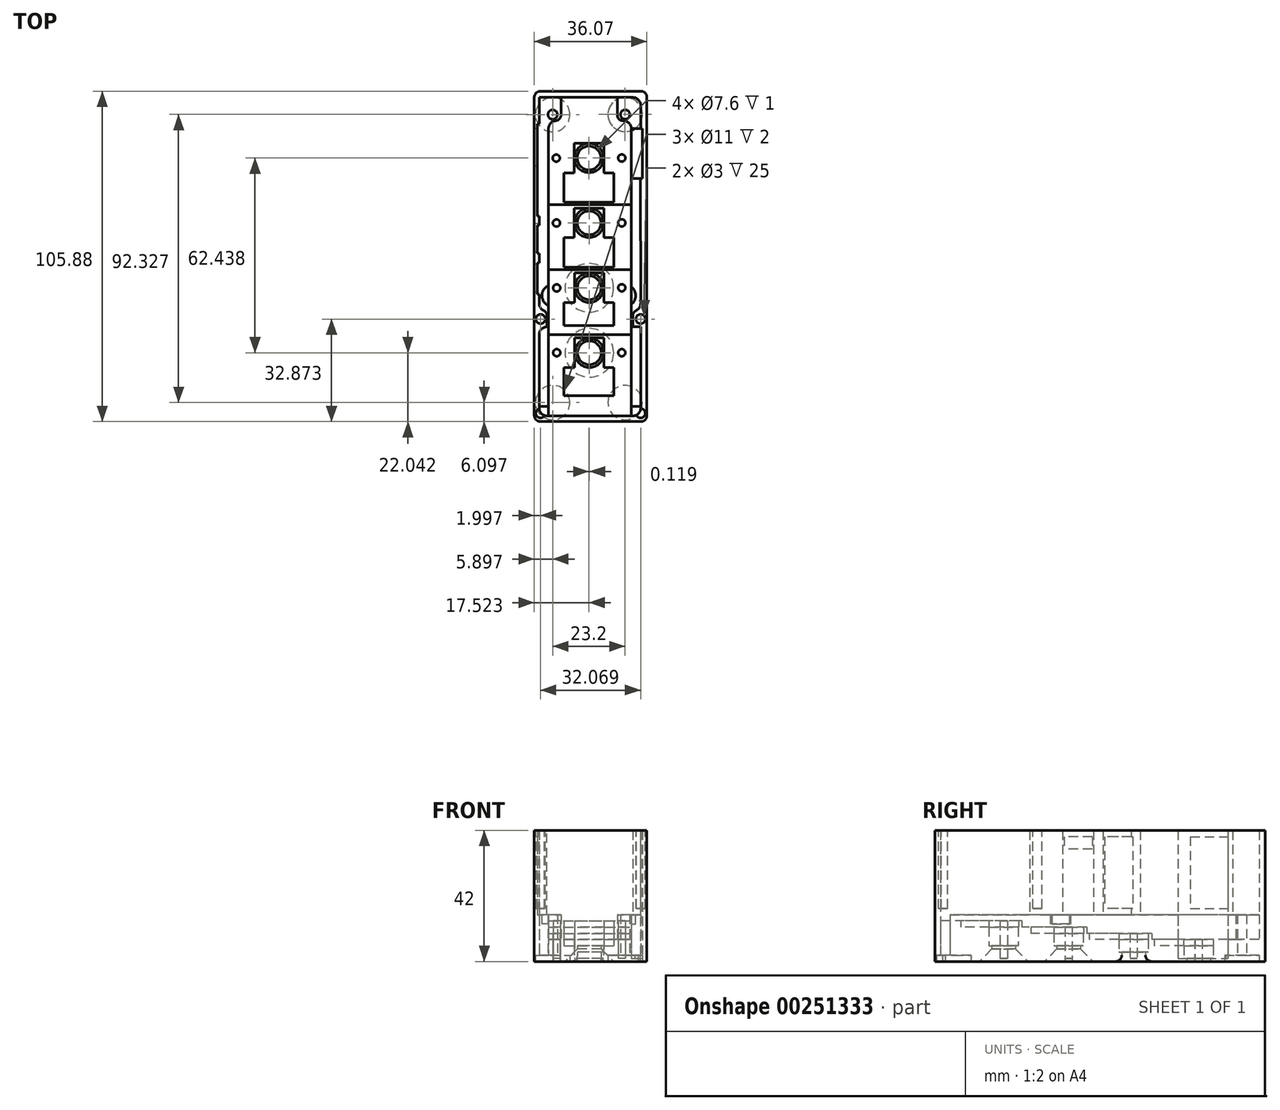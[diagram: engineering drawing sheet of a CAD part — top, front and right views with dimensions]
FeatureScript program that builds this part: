
annotation { "Feature Type Name" : "Feature", "Feature Type Description" : "" }
export const myFeature = defineFeature(function(context is Context, id is Id, definition is map)
    precondition{}
    {
        {
            var Q0;
            Q0=qCreatedBy(makeId("Top.planeOp"),FACE);
            var sketch = newSketch(context, id + "F0", { "sketchPlane" : qUnion([Q0])});
            skLineSegment(sketch, "E0.right", {"start": v(-34.07, -40) * mm, "end": v(-34.07, 40) * mm});
            skLineSegment(sketch, "E1.right", {"start": v(-32.5, -38) * mm, "end": v(-32.5, 38) * mm});
            skLineSegment(sketch, "E2.bottom", {"start": v(-32.5, 38) * mm, "end": v(-29.5, 38) * mm});
            skLineSegment(sketch, "E2.left", {"start": v(-32.5, 38) * mm, "end": v(-32.5, 34.5) * mm});
            skLineSegment(sketch, "E2.right", {"start": v(-29.5, 38) * mm, "end": v(-29.5, 34.5) * mm});
            skLineSegment(sketch, "E3.left", {"start": v(-3, 37.19) * mm, "end": v(-3, 33.69) * mm});
            skLineSegment(sketch, "E4", {"start": v(-29.5, 34.5) * mm, "end": v(-29.5, -32.3) * mm});
            skLineSegment(sketch, "E5", {"start": v(-3, 33.69) * mm, "end": v(-3, -33.11) * mm});
            skPoint(sketch, "E6.centerSnap0", {"position": v(-31, 34.5) * mm});
            skLineSegment(sketch, "E7.left", {"start": v(-34.07, -40) * mm, "end": v(-34.07, -41.8) * mm});
            skLineSegment(sketch, "E8", {"start": v(-32.5, -38) * mm, "end": v(-32.5, -40) * mm});
            skLineSegment(sketch, "E9", {"start": v(-16.57, 32.32) * mm, "end": v(-16.42, -49.3) * mm, "construction": true});
            skCircle(sketch, "E10", {"center": v(-16.47, -23) * mm, "radius": 4.7 * mm});
            skCircle(sketch, "E11", {"center": v(-16.5, -2.2) * mm, "radius": 4.7 * mm});
            skCircle(sketch, "E12", {"center": v(-16.55, 18.6) * mm, "radius": 4.7 * mm});
            skLineSegment(sketch, "E13.bottom", {"start": v(-11.72, -27.75) * mm, "end": v(-21.22, -27.75) * mm});
            skLineSegment(sketch, "E13.top", {"start": v(-11.72, -18.25) * mm, "end": v(-21.22, -18.25) * mm});
            skLineSegment(sketch, "E13.left", {"start": v(-11.72, -27.75) * mm, "end": v(-11.72, -18.25) * mm});
            skLineSegment(sketch, "E13.right", {"start": v(-21.22, -27.75) * mm, "end": v(-21.22, -18.25) * mm});
            skLineSegment(sketch, "E14.bottom", {"start": v(-11.76, -6.95) * mm, "end": v(-21.26, -6.95) * mm});
            skLineSegment(sketch, "E14.top", {"start": v(-11.76, 2.55) * mm, "end": v(-21.26, 2.55) * mm});
            skLineSegment(sketch, "E14.left", {"start": v(-11.76, -6.95) * mm, "end": v(-11.76, 2.55) * mm});
            skLineSegment(sketch, "E14.right", {"start": v(-21.26, -6.95) * mm, "end": v(-21.26, 2.55) * mm});
            skLineSegment(sketch, "E15.bottom", {"start": v(-11.8, 13.85) * mm, "end": v(-21.3, 13.85) * mm});
            skLineSegment(sketch, "E15.top", {"start": v(-11.8, 23.35) * mm, "end": v(-21.3, 23.35) * mm});
            skLineSegment(sketch, "E15.left", {"start": v(-11.8, 13.85) * mm, "end": v(-11.8, 23.35) * mm});
            skLineSegment(sketch, "E15.right", {"start": v(-21.3, 13.85) * mm, "end": v(-21.3, 23.35) * mm});
            skLineSegment(sketch, "E16.bottom", {"start": v(-24.55, 13.85) * mm, "end": v(-8.55, 13.85) * mm});
            skLineSegment(sketch, "E16.top", {"start": v(-24.55, 4.35) * mm, "end": v(-8.55, 4.35) * mm});
            skLineSegment(sketch, "E16.left", {"start": v(-24.55, 13.85) * mm, "end": v(-24.55, 4.35) * mm});
            skLineSegment(sketch, "E16.right", {"start": v(-8.55, 13.85) * mm, "end": v(-8.55, 4.35) * mm});
            skLineSegment(sketch, "E17.bottom", {"start": v(-24.55, -6.95) * mm, "end": v(-8.55, -6.95) * mm});
            skLineSegment(sketch, "E17.top", {"start": v(-24.55, -16.45) * mm, "end": v(-8.55, -16.45) * mm});
            skLineSegment(sketch, "E17.left", {"start": v(-24.55, -6.95) * mm, "end": v(-24.55, -16.45) * mm});
            skLineSegment(sketch, "E17.right", {"start": v(-8.55, -6.95) * mm, "end": v(-8.55, -16.45) * mm});
            skPoint(sketch, "E18.oppositeSnap0", {"position": v(-7.5, -35.15) * mm});
            skLineSegment(sketch, "E18.bottom", {"start": v(-24.55, -27.75) * mm, "end": v(-8.55, -27.75) * mm});
            skLineSegment(sketch, "E18.top", {"start": v(-24.55, -35.15) * mm, "end": v(-8.55, -35.15) * mm});
            skLineSegment(sketch, "E18.left", {"start": v(-24.55, -27.75) * mm, "end": v(-24.55, -35.15) * mm});
            skLineSegment(sketch, "E18.right", {"start": v(-8.55, -27.75) * mm, "end": v(-8.55, -35.15) * mm});
            skLineSegment(sketch, "E19.MirrorCS", {"start": v(-7.5, 32.3) * mm, "end": v(-7.5, 38) * mm});
            skLineSegment(sketch, "E20", {"start": v(-29.5, -32.3) * mm, "end": v(-29.5, -38) * mm});
            skLineSegment(sketch, "E21", {"start": v(-29.5, 3.6) * mm, "end": v(-3, 3.6) * mm});
            skLineSegment(sketch, "E22", {"start": v(-29.5, -17.2) * mm, "end": v(-3, -17.2) * mm});
            skCircle(sketch, "E23", {"center": v(-16.55, 18.6) * mm, "radius": 3.8 * mm});
            skCircle(sketch, "E24", {"center": v(-16.5, -2.2) * mm, "radius": 3.8 * mm});
            skCircle(sketch, "E25", {"center": v(-16.47, -23) * mm, "radius": 3.8 * mm});
            skPoint(sketch, "E26.endSnap0", {"position": v(-29.5, -35.15) * mm});
            skLineSegment(sketch, "E27", {"start": v(-29.5, -38) * mm, "end": v(-29.5, -40) * mm});
            skCircle(sketch, "E28", {"center": v(-6.05, 18.6) * mm, "radius": 1.15 * mm});
            skCircle(sketch, "E29", {"center": v(-6.05, -2.2) * mm, "radius": 1.15 * mm});
            skCircle(sketch, "E30", {"center": v(-6.05, -23) * mm, "radius": 1.15 * mm});
            skCircle(sketch, "E31.MirrorC", {"center": v(-27.05, 18.56) * mm, "radius": 1.15 * mm});
            skCircle(sketch, "E32.MirrorC", {"center": v(-26.97, -2.24) * mm, "radius": 1.15 * mm});
            skCircle(sketch, "E33.MirrorC", {"center": v(-26.89, -23.04) * mm, "radius": 1.15 * mm});
            skLineSegment(sketch, "E34.bottom", {"start": v(-7.5, 38) * mm, "end": v(-3, 38) * mm});
            skLineSegment(sketch, "E34.top", {"start": v(-7.5, 30.5) * mm, "end": v(-3, 30.5) * mm});
            skLineSegment(sketch, "E34.left", {"start": v(-7.5, 38) * mm, "end": v(-7.5, 30.5) * mm});
            skLineSegment(sketch, "E34.right", {"start": v(-3, 38) * mm, "end": v(-3, 30.5) * mm});
            skLineSegment(sketch, "E35.bottom", {"start": v(-32.5, 38) * mm, "end": v(-26.5, 38) * mm});
            skLineSegment(sketch, "E35.left", {"start": v(-32.5, 38) * mm, "end": v(-32.5, 30.5) * mm});
            skCircle(sketch, "E36", {"center": v(-28.17, 32.5) * mm, "radius": 1.5 * mm});
            skCircle(sketch, "E37.MirrorC", {"center": v(-4.97, 32.54) * mm, "radius": 1.5 * mm});
            skLineSegment(sketch, "E38.bottom", {"start": v(-32.5, 38) * mm, "end": v(-25.5, 38) * mm});
            skLineSegment(sketch, "E38.top", {"start": v(-32.5, 30.52) * mm, "end": v(-25.5, 30.52) * mm});
            skLineSegment(sketch, "E38.left", {"start": v(-32.5, 38) * mm, "end": v(-32.5, 30.52) * mm});
            skLineSegment(sketch, "E38.right", {"start": v(-25.5, 38) * mm, "end": v(-25.5, 30.52) * mm});
            skLineSegment(sketch, "E39.bottom", {"start": v(-32.5, -3) * mm, "end": v(-33.1, -3) * mm});
            skLineSegment(sketch, "E39.top", {"start": v(-32.5, -12) * mm, "end": v(-33.1, -12) * mm});
            skLineSegment(sketch, "E39.left", {"start": v(-32.5, -3) * mm, "end": v(-32.5, -12) * mm});
            skLineSegment(sketch, "E39.right", {"start": v(-33.1, -3) * mm, "end": v(-33.1, -12) * mm});
            skLineSegment(sketch, "E40.bottom", {"start": v(-32.5, -15) * mm, "end": v(-33.1, -15) * mm});
            skLineSegment(sketch, "E40.top", {"start": v(-32.5, -25) * mm, "end": v(-33.1, -25) * mm});
            skLineSegment(sketch, "E40.left", {"start": v(-32.5, -15) * mm, "end": v(-32.5, -25) * mm});
            skLineSegment(sketch, "E40.right", {"start": v(-33.1, -15) * mm, "end": v(-33.1, -25) * mm});
            skLineSegment(sketch, "E41.bottom", {"start": v(-32.5, 0) * mm, "end": v(-33.1, 0) * mm});
            skLineSegment(sketch, "E41.top", {"start": v(-32.5, 29.5) * mm, "end": v(-33.1, 29.5) * mm});
            skLineSegment(sketch, "E41.left", {"start": v(-32.5, 0) * mm, "end": v(-32.5, 29.5) * mm});
            skLineSegment(sketch, "E41.right", {"start": v(-33.1, 0) * mm, "end": v(-33.1, 29.5) * mm});
            skLineSegment(sketch, "E42", {"start": v(-34.07, 40) * mm, "end": v(-0.07, 40) * mm});
            skLineSegment(sketch, "E43", {"start": v(-0.07, 40) * mm, "end": v(0, -43.3) * mm});
            skLineSegment(sketch, "E44", {"start": v(-1.5, 38) * mm, "end": v(-32.5, 38) * mm});
            skLineSegment(sketch, "E45", {"start": v(-32.5, 38) * mm, "end": v(0, 38) * mm});
            skLineSegment(sketch, "E46", {"start": v(0, 38) * mm, "end": v(0, -40) * mm});
            skLineSegment(sketch, "E47", {"start": v(2, -41.8) * mm, "end": v(2, 40) * mm});
            skLineSegment(sketch, "E48", {"start": v(2, 40) * mm, "end": v(-34.07, 40) * mm});
            skLineSegment(sketch, "E49", {"start": v(-3, -33.11) * mm, "end": v(-3, -40.81) * mm});
            skLineSegment(sketch, "E50", {"start": v(-29.5, -38) * mm, "end": v(-3, -38) * mm});
            skLineSegment(sketch, "E51", {"start": v(-3, -38) * mm, "end": v(-3, -62) * mm});
            skLineSegment(sketch, "E52", {"start": v(-29.5, -62) * mm, "end": v(-29.5, -40) * mm});
            skLineSegment(sketch, "E53", {"start": v(-32.5, -40) * mm, "end": v(-32.5, -64.04) * mm});
            skLineSegment(sketch, "E54", {"start": v(-32.5, -64.04) * mm, "end": v(0, -64.04) * mm});
            skLineSegment(sketch, "E55", {"start": v(0, -64.04) * mm, "end": v(0, -43.3) * mm});
            skLineSegment(sketch, "E56", {"start": v(2, -41.8) * mm, "end": v(2, -65.87) * mm});
            skLineSegment(sketch, "E57", {"start": v(2, -65.87) * mm, "end": v(-34.07, -65.88) * mm});
            skLineSegment(sketch, "E58", {"start": v(-34.07, -65.88) * mm, "end": v(-34.07, -41.8) * mm});
            skLineSegment(sketch, "E59.bottom", {"start": v(-24.55, -48.55) * mm, "end": v(-8.55, -48.55) * mm});
            skLineSegment(sketch, "E59.top", {"start": v(-24.55, -57.55) * mm, "end": v(-8.55, -57.55) * mm});
            skLineSegment(sketch, "E59.left", {"start": v(-24.55, -48.55) * mm, "end": v(-24.55, -57.55) * mm});
            skLineSegment(sketch, "E59.right", {"start": v(-8.55, -48.55) * mm, "end": v(-8.55, -57.55) * mm});
            skLineSegment(sketch, "E60", {"start": v(-21.22, -39.06) * mm, "end": v(-21.2, -48.55) * mm});
            skCircle(sketch, "E61", {"center": v(-6.05, -43.8) * mm, "radius": 1.15 * mm});
            skCircle(sketch, "E62", {"center": v(-26.89, -43.8) * mm, "radius": 1.15 * mm});
            skLineSegment(sketch, "E63", {"start": v(-3, 28) * mm, "end": v(0, 28) * mm});
            skLineSegment(sketch, "E64", {"start": v(-3, 12) * mm, "end": v(0, 12) * mm});
            skLineSegment(sketch, "E65", {"start": v(0, 12) * mm, "end": v(0.5, 12) * mm});
            skLineSegment(sketch, "E66", {"start": v(0.5, 12) * mm, "end": v(0.5, 28) * mm});
            skLineSegment(sketch, "E67", {"start": v(0.5, 28) * mm, "end": v(0, 28) * mm});
            skLineSegment(sketch, "E68", {"start": v(-29.5, -62) * mm, "end": v(-29.5, -64.04) * mm});
            skLineSegment(sketch, "E69", {"start": v(-3, -62) * mm, "end": v(-3, -64.04) * mm});
            skLineSegment(sketch, "E70", {"start": v(-21.22, -39.06) * mm, "end": v(-11.72, -39.04) * mm});
            skLineSegment(sketch, "E71", {"start": v(-11.72, -39.04) * mm, "end": v(-11.72, -48.55) * mm});
            skCircle(sketch, "E72", {"center": v(-16.43, -43.84) * mm, "radius": 4.7 * mm});
            skCircle(sketch, "E73", {"center": v(-16.43, -43.84) * mm, "radius": 3.8 * mm});
            skLineSegment(sketch, "E74.bottom", {"start": v(-32.5, -30.5) * mm, "end": v(-30, -30.5) * mm});
            skLineSegment(sketch, "E74.top", {"start": v(-32.5, -35.5) * mm, "end": v(-30, -35.5) * mm});
            skLineSegment(sketch, "E74.left", {"start": v(-32.5, -30.5) * mm, "end": v(-32.5, -35.5) * mm});
            skLineSegment(sketch, "E74.right", {"start": v(-30, -30.5) * mm, "end": v(-30, -35.5) * mm});
            skLineSegment(sketch, "E75.bottom", {"start": v(-0.01, -30.5) * mm, "end": v(-2.51, -30.5) * mm});
            skLineSegment(sketch, "E75.top", {"start": v(-0.01, -35.5) * mm, "end": v(-2.51, -35.5) * mm});
            skLineSegment(sketch, "E75.left", {"start": v(-0.01, -30.5) * mm, "end": v(-0.01, -35.5) * mm});
            skLineSegment(sketch, "E75.right", {"start": v(-2.51, -30.5) * mm, "end": v(-2.51, -35.5) * mm});
            skLineSegment(sketch, "E76.bottom", {"start": v(-29.5, -64.04) * mm, "end": v(-32.5, -64.04) * mm});
            skLineSegment(sketch, "E76.top", {"start": v(-29.5, -61.04) * mm, "end": v(-32.5, -61.04) * mm});
            skLineSegment(sketch, "E76.left", {"start": v(-29.5, -64.04) * mm, "end": v(-29.5, -61.04) * mm});
            skLineSegment(sketch, "E76.right", {"start": v(-32.5, -64.04) * mm, "end": v(-32.5, -61.04) * mm});
            skLineSegment(sketch, "E77.bottom", {"start": v(-3, -64.04) * mm, "end": v(0, -64.04) * mm});
            skLineSegment(sketch, "E78.top", {"start": v(0, -61.04) * mm, "end": v(-3, -61.04) * mm});
            skLineSegment(sketch, "E78.right", {"start": v(-3, -64.04) * mm, "end": v(-3, -61.04) * mm});
            skSolve(sketch);
        }
        {
            var Q0;
            Q0=makeQuery(id+"F0.imprint","IMPRINT",FACE,{"disambiguationData":[TD([[makeQuery(id+"F0.imprint","IMPRINT",EDGE,{"derivedFrom":sQuery(id+"F0.wireOp",EDGE,"MCkaOSE9-IhCf-8ool-gKyj-9XubC7RGo3ym")}),1.0]])]});
            var Q1;
            Q1=makeQuery(id+"F0.imprint","IMPRINT",FACE,{"disambiguationData":[TD([[makeQuery(id+"F0.imprint","IMPRINT",EDGE,{"derivedFrom":sQuery(id+"F0.wireOp",EDGE,"7725986d-b48c-4c88-8d1c-f6a26a28f13d0.MirrorC")}),-1.0]])]});
            var Q2;
            Q2=makeQuery(id+"F0.imprint","IMPRINT",FACE,{"disambiguationData":[TD([[makeQuery(id+"F0.imprint","IMPRINT",EDGE,{"derivedFrom":sQuery(id+"F0.wireOp",EDGE,"59a4a79b-c9f1-4cd0-aec9-fd9c437c135d0.MirrorC")}),-1.0]])]});
            var Q3;
            Q3=makeQuery(id+"F0.imprint","IMPRINT",FACE,{"disambiguationData":[TD([[makeQuery(id+"F0.imprint","IMPRINT",EDGE,{"derivedFrom":sQuery(id+"F0.wireOp",EDGE,"a35e930e-65d3-4072-b997-69f2f612cff60.MirrorC")}),-1.0]])]});
            var Q4;
            Q4=makeQuery(id+"F0.imprint","IMPRINT",FACE,{"disambiguationData":[TD([[makeQuery(id+"F0.imprint","IMPRINT",EDGE,{"derivedFrom":sQuery(id+"F0.wireOp",EDGE,"HDPAf1v4-qRVW-bhF8-Vumt-nlOvChXnVlKt")}),1.0]])]});
            var Q5;
            Q5=makeQuery(id+"F0.imprint","IMPRINT",FACE,{"disambiguationData":[TD([[makeQuery(id+"F0.imprint","IMPRINT",EDGE,{"derivedFrom":sQuery(id+"F0.wireOp",EDGE,"2aBwPfGq-D8N3-xRyg-Atcc-50ip9IBR1yyq")}),1.0]])]});
            var Q6;
            Q6=makeQuery(id+"F0.imprint","IMPRINT",FACE,{"disambiguationData":[TD([[makeQuery(id+"F0.imprint","IMPRINT",EDGE,{"derivedFrom":sQuery(id+"F0.wireOp",EDGE,"3206e315-043b-4236-9ddf-d42e6e429b7f0.MirrorC")}),-1.0]])]});
            var Q7;
            Q7=makeQuery(id+"F0.imprint","IMPRINT",FACE,{"disambiguationData":[TD([[makeQuery(id+"F0.imprint","IMPRINT",EDGE,{"derivedFrom":sQuery(id+"F0.wireOp",EDGE,"92c6dff3-5c9b-4808-a7d1-03b6115bcbae0.MirrorC")}),-1.0]])]});
            var Q8;
            Q8=makeQuery(id+"F0.imprint","IMPRINT",FACE,{"disambiguationData":[TD([[makeQuery(id+"F0.imprint","IMPRINT",EDGE,{"derivedFrom":sQuery(id+"F0.wireOp",EDGE,"0e0c7713-d091-498b-95ae-dc4961e39de90.MirrorC")}),1.0]])]});
            var Q9;
            Q9=makeQuery(id+"F0.imprint","IMPRINT",FACE,{"disambiguationData":[TD([[makeQuery(id+"F0.imprint","IMPRINT",EDGE,{"derivedFrom":sQuery(id+"F0.wireOp",EDGE,"047f7080-29e6-4cd1-92cd-44153eb5f8b00.MirrorC")}),1.0]])]});
            var Q10;
            Q10=makeQuery(id+"F0.imprint","IMPRINT",FACE,{"disambiguationData":[TD([[makeQuery(id+"F0.imprint","IMPRINT",EDGE,{"derivedFrom":sQuery(id+"F0.wireOp",EDGE,"qaKc8OcJ-KyJv-MFnS-BuUQ-nGE731uP4IVA")}),1.0]])]});
            var Q11;
            Q11=makeQuery(id+"F0.imprint","IMPRINT",FACE,{"disambiguationData":[TD([[makeQuery(id+"F0.imprint","IMPRINT",EDGE,{"derivedFrom":sQuery(id+"F0.wireOp",EDGE,"yCcRbTM1-u1l2-tKAz-wE2g-ceJNBIoqUPmB")}),1.0]])]});
            var Q12;
            Q12=makeQuery(id+"F0.imprint","IMPRINT",FACE,{"disambiguationData":[TD([[makeQuery(id+"F0.imprint","IMPRINT",EDGE,{"derivedFrom":sQuery(id+"F0.wireOp",EDGE,"bcc14edc-98c6-48ef-b5fb-fc75301954bd0.MirrorC")}),-1.0]])]});
            var Q13;
            Q13=makeQuery(id+"F0.imprint","IMPRINT",FACE,{"disambiguationData":[TD([[makeQuery(id+"F0.imprint","IMPRINT",EDGE,{"derivedFrom":sQuery(id+"F0.wireOp",EDGE,"1503a08b-597c-4ee8-9578-b5f4a8ded7c60.MirrorC")}),-1.0]])]});
            var Q14;
            Q14=makeQuery(id+"F0.imprint","IMPRINT",FACE,{"disambiguationData":[TD([[makeQuery(id+"F0.imprint","IMPRINT",EDGE,{"derivedFrom":sQuery(id+"F0.wireOp",EDGE,"0ae987a1-7970-4579-8789-16a3eeb237370.MirrorC")}),-1.0]])]});
            var Q15;
            Q15=makeQuery(id+"F0.imprint","IMPRINT",FACE,{"disambiguationData":[TD([[makeQuery(id+"F0.imprint","IMPRINT",EDGE,{"derivedFrom":sQuery(id+"F0.wireOp",EDGE,"aRgkTEOP-yxzU-5Pec-RQmy-s6JdjeDGBb0V")}),1.0]])]});
            var Q16;
            Q16=makeQuery(id+"F0.imprint","IMPRINT",FACE,{"disambiguationData":[TD([[makeQuery(id+"F0.imprint","IMPRINT",EDGE,{"derivedFrom":sQuery(id+"F0.wireOp",EDGE,"0680d632-f290-4353-81a7-de359aa27e5b0.MirrorC")}),-1.0]])]});
            var Q17;
            Q17=makeQuery(id+"F0.imprint","IMPRINT",FACE,{"disambiguationData":[TD([[makeQuery(id+"F0.imprint","IMPRINT",EDGE,{"derivedFrom":sQuery(id+"F0.wireOp",EDGE,"c30eccc4-6726-4d0a-a499-8a75d68b827e0.MirrorC")}),1.0]])]});
            var Q18;
            {var subQ0=sQuery(id+"F0.wireOp",EDGE,"iNITCdC1-V6Gu-A9aK-RxGo-pSBVGAeka9JE");var subQ1=sQuery(id+"F0.wireOp",EDGE,"E3.bottom");var subQ2=makeQuery(id+"F0.imprint","INTERSECT",VERTEX,{"disambiguationData":[OD(0.0)],"derivedFrom":[subQ1,subQ0]});Q18=makeQuery(id+"F0.imprint","IMPRINT",FACE,{"disambiguationData":[TD([[makeQuery(id+"F0.imprint","IMPRINT",EDGE,{"disambiguationData":[TD([[subQ2,-1.0]])],"derivedFrom":subQ1}),-1.0]])]});}
            var Q19;
            {var subQ0=sQuery(id+"F0.wireOp",EDGE,"iNITCdC1-V6Gu-A9aK-RxGo-pSBVGAeka9JE");var subQ1=sQuery(id+"F0.wireOp",EDGE,"E3.bottom");var subQ2=makeQuery(id+"F0.imprint","INTERSECT",VERTEX,{"disambiguationData":[OD(0.0)],"derivedFrom":[subQ1,subQ0]});Q19=makeQuery(id+"F0.imprint","IMPRINT",FACE,{"disambiguationData":[TD([[makeQuery(id+"F0.imprint","IMPRINT",EDGE,{"disambiguationData":[TD([[subQ2,-1.0]])],"derivedFrom":subQ1}),1.0]])]});}
            var Q20;
            {var subQ3=sQuery(id+"F0.wireOp",EDGE,"b4bfbbc8-bfb4-457f-a4ea-ce27dee804a20.MirrorCS");Q20=makeQuery(id+"F0.imprint","IMPRINT",FACE,{"disambiguationData":[TD([[makeQuery(id+"F0.imprint","IMPRINT",EDGE,{"derivedFrom":subQ3}),-1.0]])]});}
            var Q21;
            {var subQ3=sQuery(id+"F0.wireOp",EDGE,"373be7a7-a180-4500-8c4f-fb7f05af98d20.MirrorCS");Q21=makeQuery(id+"F0.imprint","IMPRINT",FACE,{"disambiguationData":[TD([[makeQuery(id+"F0.imprint","IMPRINT",EDGE,{"derivedFrom":subQ3}),1.0]])]});}
            var Q22;
            {var subQ3=sQuery(id+"F0.wireOp",EDGE,"8c54c704-6125-45c6-a136-09c856472eb80.MirrorCS");Q22=makeQuery(id+"F0.imprint","IMPRINT",FACE,{"disambiguationData":[TD([[makeQuery(id+"F0.imprint","IMPRINT",EDGE,{"derivedFrom":subQ3}),-1.0]])]});}
            var Q23;
            {var subQ3=sQuery(id+"F0.wireOp",EDGE,"AKNDvyLU-ZjiQ-5B7P-d9uo-GwxmQcMPWuOC");Q23=makeQuery(id+"F0.imprint","IMPRINT",FACE,{"disambiguationData":[TD([[makeQuery(id+"F0.imprint","IMPRINT",EDGE,{"derivedFrom":subQ3}),1.0]])]});}
            var Q24;
            Q24=makeQuery(id+"F0.imprint","IMPRINT",FACE,{"disambiguationData":[TD([[makeQuery(id+"F0.imprint","IMPRINT",EDGE,{"derivedFrom":sQuery(id+"F0.wireOp",EDGE,"1iW9IMMN-0FES-SWrY-3OQA-0guGBfABkkHx.bottom")}),-1.0]])]});
            var Q25;
            {var subQ0=sQuery(id+"F0.wireOp",EDGE,"7e7d4f16-1e5e-4483-a9e2-a789900bc4030.MirrorC");var subQ1=sQuery(id+"F0.wireOp",EDGE,"c35836a9-8250-4898-909e-bbcbb419c5620.MirrorCS");var subQ2=makeQuery(id+"F0.imprint","INTERSECT",VERTEX,{"disambiguationData":[OD(0.0)],"derivedFrom":[subQ1,subQ0]});Q25=makeQuery(id+"F0.imprint","IMPRINT",FACE,{"disambiguationData":[TD([[makeQuery(id+"F0.imprint","IMPRINT",EDGE,{"disambiguationData":[TD([[subQ2,-1.0]])],"derivedFrom":subQ1}),1.0]])]});}
            var Q26;
            {var subQ0=sQuery(id+"F0.wireOp",EDGE,"7e7d4f16-1e5e-4483-a9e2-a789900bc4030.MirrorC");var subQ1=sQuery(id+"F0.wireOp",EDGE,"c35836a9-8250-4898-909e-bbcbb419c5620.MirrorCS");var subQ2=makeQuery(id+"F0.imprint","INTERSECT",VERTEX,{"disambiguationData":[OD(0.0)],"derivedFrom":[subQ1,subQ0]});Q26=makeQuery(id+"F0.imprint","IMPRINT",FACE,{"disambiguationData":[TD([[makeQuery(id+"F0.imprint","IMPRINT",EDGE,{"disambiguationData":[TD([[subQ2,-1.0]])],"derivedFrom":subQ1}),-1.0]])]});}
            var Q27;
            {var subQ0=sQuery(id+"F0.wireOp",EDGE,"KXApSkYF-fskY-EpyV-lEOU-AstEEemZVb44");var subQ1=sQuery(id+"F0.wireOp",EDGE,"1iW9IMMN-0FES-SWrY-3OQA-0guGBfABkkHx.bottom");var subQ2=makeQuery(id+"F0.imprint","INTERSECT",VERTEX,{"derivedFrom":[subQ1,subQ0]});Q27=makeQuery(id+"F0.imprint","IMPRINT",FACE,{"disambiguationData":[TD([[makeQuery(id+"F0.imprint","IMPRINT",EDGE,{"disambiguationData":[TD([[subQ2,-1.0]])],"derivedFrom":subQ1}),1.0]])]});}
            var Q28;
            Q28=makeQuery(id+"F0.imprint","IMPRINT",FACE,{"disambiguationData":[TD([[makeQuery(id+"F0.imprint","IMPRINT",EDGE,{"derivedFrom":sQuery(id+"F0.wireOp",EDGE,"E12")}),1.0]])]});
            var Q29;
            Q29=makeQuery(id+"F0.imprint","IMPRINT",FACE,{"disambiguationData":[TD([[makeQuery(id+"F0.imprint","IMPRINT",EDGE,{"derivedFrom":sQuery(id+"F0.wireOp",EDGE,"E29")}),1.0]])]});
            var Q30;
            Q30=makeQuery(id+"F0.imprint","IMPRINT",FACE,{"disambiguationData":[TD([[makeQuery(id+"F0.imprint","IMPRINT",EDGE,{"derivedFrom":sQuery(id+"F0.wireOp",EDGE,"E28")}),1.0]])]});
            var Q31;
            Q31=makeQuery(id+"F0.imprint","IMPRINT",FACE,{"disambiguationData":[TD([[makeQuery(id+"F0.imprint","IMPRINT",EDGE,{"derivedFrom":sQuery(id+"F0.wireOp",EDGE,"E31.MirrorC")}),-1.0]])]});
            var Q32;
            Q32=makeQuery(id+"F0.imprint","IMPRINT",FACE,{"disambiguationData":[TD([[makeQuery(id+"F0.imprint","IMPRINT",EDGE,{"derivedFrom":sQuery(id+"F0.wireOp",EDGE,"E32.MirrorC")}),-1.0]])]});
            var Q33;
            Q33=makeQuery(id+"F0.imprint","IMPRINT",FACE,{"disambiguationData":[TD([[makeQuery(id+"F0.imprint","IMPRINT",EDGE,{"derivedFrom":sQuery(id+"F0.wireOp",EDGE,"E33.MirrorC")}),-1.0]])]});
            var Q34;
            Q34=makeQuery(id+"F0.imprint","IMPRINT",FACE,{"disambiguationData":[TD([[makeQuery(id+"F0.imprint","IMPRINT",EDGE,{"derivedFrom":sQuery(id+"F0.wireOp",EDGE,"E30")}),1.0]])]});
            var Q35;
            Q35=makeQuery(id+"F0.imprint","IMPRINT",FACE,{"disambiguationData":[TD([[makeQuery(id+"F0.imprint","IMPRINT",EDGE,{"derivedFrom":sQuery(id+"F0.wireOp",EDGE,"c25f4905-031d-4495-adcf-e8cfd4a8596b0.MirrorC")}),-1.0]])]});
            var Q36;
            {var subQ1=sQuery(id+"F0.wireOp",EDGE,"E2.right");var subQ3=sQuery(id+"F0.wireOp",EDGE,"e070aa0f-a60b-4e3b-b1ba-bdaac02ee6940.MirrorC");var subQ4=makeQuery(id+"F0.imprint","INTERSECT",VERTEX,{"derivedFrom":[subQ1,subQ3]});Q36=makeQuery(id+"F0.imprint","IMPRINT",FACE,{"disambiguationData":[TD([[makeQuery(id+"F0.imprint","IMPRINT",EDGE,{"disambiguationData":[TD([[subQ4,-1.0]])],"derivedFrom":subQ3}),-1.0]])]});}
            var Q37;
            {var subQ1=sQuery(id+"F0.wireOp",EDGE,"E2.top");var subQ3=sQuery(id+"F0.wireOp",EDGE,"e070aa0f-a60b-4e3b-b1ba-bdaac02ee6940.MirrorC");var subQ4=makeQuery(id+"F0.imprint","INTERSECT",VERTEX,{"derivedFrom":[subQ1,subQ3]});Q37=makeQuery(id+"F0.imprint","IMPRINT",FACE,{"disambiguationData":[TD([[makeQuery(id+"F0.imprint","IMPRINT",EDGE,{"disambiguationData":[TD([[subQ4,1.0]])],"derivedFrom":subQ3}),-1.0]])]});}
            var Q38;
            {var subQ1=sQuery(id+"F0.wireOp",EDGE,"E2.top");var subQ3=sQuery(id+"F0.wireOp",EDGE,"e070aa0f-a60b-4e3b-b1ba-bdaac02ee6940.MirrorC");var subQ4=makeQuery(id+"F0.imprint","INTERSECT",VERTEX,{"derivedFrom":[subQ1,subQ3]});Q38=makeQuery(id+"F0.imprint","IMPRINT",FACE,{"disambiguationData":[TD([[makeQuery(id+"F0.imprint","IMPRINT",EDGE,{"disambiguationData":[TD([[subQ4,-1.0]])],"derivedFrom":subQ3}),-1.0]])]});}
            var Q39;
            {var subQ0=sQuery(id+"F0.wireOp",EDGE,"E63");var subQ1=sQuery(id+"F0.wireOp",EDGE,"E5");var subQ2=makeQuery(id+"F0.imprint","INTERSECT",VERTEX,{"derivedFrom":[subQ1,subQ0]});Q39=makeQuery(id+"F0.imprint","IMPRINT",FACE,{"disambiguationData":[TD([[makeQuery(id+"F0.imprint","IMPRINT",EDGE,{"disambiguationData":[TD([[subQ2,-1.0]])],"derivedFrom":subQ1}),1.0]])]});}
            var Q40;
            Q40=makeQuery(id+"F0.imprint","IMPRINT",FACE,{"disambiguationData":[TD([[makeQuery(id+"F0.imprint","IMPRINT",EDGE,{"derivedFrom":sQuery(id+"F0.wireOp",EDGE,"E61")}),1.0]])]});
            var Q41;
            Q41=makeQuery(id+"F0.imprint","IMPRINT",FACE,{"disambiguationData":[TD([[makeQuery(id+"F0.imprint","IMPRINT",EDGE,{"derivedFrom":sQuery(id+"F0.wireOp",EDGE,"E62")}),1.0]])]});
            var Q42;
            {var subQ2=sQuery(id+"F0.wireOp",EDGE,"E65");Q42=makeQuery(id+"F0.imprint","IMPRINT",FACE,{"disambiguationData":[TD([[makeQuery(id+"F0.imprint","IMPRINT",EDGE,{"derivedFrom":subQ2}),1.0]])]});}
            var Q43;
            {var subQ0=sQuery(id+"F0.wireOp",EDGE,"E63");var subQ1=sQuery(id+"F0.wireOp",EDGE,"E43");var subQ2=makeQuery(id+"F0.imprint","INTERSECT",VERTEX,{"derivedFrom":[subQ1,subQ0]});Q43=makeQuery(id+"F0.imprint","IMPRINT",FACE,{"disambiguationData":[TD([[makeQuery(id+"F0.imprint","IMPRINT",EDGE,{"disambiguationData":[TD([[subQ2,-1.0]])],"derivedFrom":subQ1}),1.0]])]});}
            extrude(context, id + "F1", {"entities" : qUnion([Q0, Q1, Q2, Q3, Q4, Q5, Q6, Q7, Q8, Q9, Q10, Q11, Q12, Q13, Q14, Q15, Q16, Q17, Q18, Q19, Q20, Q21, Q22, Q23, Q24, Q25, Q26, Q27, Q28, Q29, Q30, Q31, Q32, Q33, Q34, Q35, Q36, Q37, Q38, Q39, Q40, Q41, Q42, Q43]), "depth" : 1 * mm});
        }
        {
            var Q0;
            Q0=makeQuery(id+"F0.imprint","IMPRINT",FACE,{"disambiguationData":[TD([[makeQuery(id+"F0.imprint","IMPRINT",EDGE,{"derivedFrom":sQuery(id+"F0.wireOp",EDGE,"MCkaOSE9-IhCf-8ool-gKyj-9XubC7RGo3ym")}),-1.0]])]});
            var Q1;
            {var subQ0=sQuery(id+"F0.wireOp",EDGE,"a23ef61d-e4c0-4117-a61e-7b1d0cea14370.MirrorCS");Q1=makeQuery(id+"F0.imprint","IMPRINT",FACE,{"disambiguationData":[TD([[makeQuery(id+"F0.imprint","IMPRINT",EDGE,{"derivedFrom":subQ0}),1.0]])]});}
            var Q2;
            Q2=makeQuery(id+"F0.imprint","IMPRINT",FACE,{"disambiguationData":[TD([[makeQuery(id+"F0.imprint","IMPRINT",EDGE,{"derivedFrom":sQuery(id+"F0.wireOp",EDGE,"wGd95vYe-XLKb-HGh0-dKvB-zlWKZVMUEUro")}),1.0]])]});
            var Q3;
            Q3=makeQuery(id+"F0.imprint","IMPRINT",FACE,{"disambiguationData":[TD([[makeQuery(id+"F0.imprint","IMPRINT",EDGE,{"derivedFrom":sQuery(id+"F0.wireOp",EDGE,"f0b77cb1-a0e4-4b6e-afd7-26acb4b0023c0.MirrorC")}),1.0]])]});
            var Q4;
            Q4=makeQuery(id+"F0.imprint","IMPRINT",FACE,{"disambiguationData":[TD([[makeQuery(id+"F0.imprint","IMPRINT",EDGE,{"derivedFrom":sQuery(id+"F0.wireOp",EDGE,"E11")}),1.0]])]});
            extrude(context, id + "F2", {"entities" : qUnion([Q0, Q1, Q2, Q3, Q4]), "operationType" : NewBodyOperationType.ADD, "depth" : 3 * mm});
        }
        {
            var Q0;
            Q0=makeQuery(id+"F0.imprint","IMPRINT",FACE,{"disambiguationData":[TD([[makeQuery(id+"F0.imprint","IMPRINT",EDGE,{"derivedFrom":sQuery(id+"F0.wireOp",EDGE,"r0QWlDTO-47mD-Vlet-8Egj-5xwrSyrvAgKR.bottom")}),-1.0]])]});
            var Q1;
            Q1=makeQuery(id+"F0.imprint","IMPRINT",FACE,{"disambiguationData":[TD([[makeQuery(id+"F0.imprint","IMPRINT",EDGE,{"derivedFrom":sQuery(id+"F0.wireOp",EDGE,"d06qtbmx-Z072-KO1i-DPNR-y8eWfwE2gxHA")}),-1.0]])]});
            var Q2;
            Q2=makeQuery(id+"F0.imprint","IMPRINT",FACE,{"disambiguationData":[TD([[makeQuery(id+"F0.imprint","IMPRINT",EDGE,{"derivedFrom":sQuery(id+"F0.wireOp",EDGE,"a992d41f-a5af-413a-96a1-0771223221050.MirrorCS")}),1.0]])]});
            var Q3;
            Q3=makeQuery(id+"F0.imprint","IMPRINT",FACE,{"disambiguationData":[TD([[makeQuery(id+"F0.imprint","IMPRINT",EDGE,{"derivedFrom":sQuery(id+"F0.wireOp",EDGE,"1432eec9-fd65-44fb-b7b7-fc5124fc1dc10.MirrorC")}),1.0]])]});
            var Q4;
            Q4=makeQuery(id+"F0.imprint","IMPRINT",FACE,{"disambiguationData":[TD([[makeQuery(id+"F0.imprint","IMPRINT",EDGE,{"derivedFrom":sQuery(id+"F0.wireOp",EDGE,"E17.top")}),1.0]])]});
            var Q5;
            Q5=makeQuery(id+"F0.imprint","IMPRINT",FACE,{"disambiguationData":[TD([[makeQuery(id+"F0.imprint","IMPRINT",EDGE,{"derivedFrom":sQuery(id+"F0.wireOp",EDGE,"E11")}),-1.0]])]});
            extrude(context, id + "F3", {"entities" : qUnion([Q0, Q1, Q2, Q3, Q4, Q5]), "operationType" : NewBodyOperationType.ADD, "depth" : 7 * mm});
        }
        {
            var Q0;
            {var subQ5=sQuery(id+"F0.wireOp",EDGE,"dCaY3Rtk-azul-797X-e86Q-lJCboUe5wdhB");Q0=makeQuery(id+"F0.imprint","IMPRINT",FACE,{"disambiguationData":[TD([[makeQuery(id+"F0.imprint","IMPRINT",EDGE,{"derivedFrom":subQ5}),-1.0]])]});}
            var Q1;
            {var subQ6=sQuery(id+"F0.wireOp",EDGE,"02aa9cdb-e34c-40cf-9694-9bee0baae9440.MirrorCS");Q1=makeQuery(id+"F0.imprint","IMPRINT",FACE,{"disambiguationData":[TD([[makeQuery(id+"F0.imprint","IMPRINT",EDGE,{"derivedFrom":subQ6}),1.0]])]});}
            var Q2;
            Q2=makeQuery(id+"F0.imprint","IMPRINT",FACE,{"disambiguationData":[TD([[makeQuery(id+"F0.imprint","IMPRINT",EDGE,{"derivedFrom":sQuery(id+"F0.wireOp",EDGE,"E14.top")}),-1.0]])]});
            extrude(context, id + "F4", {"entities" : qUnion([Q0, Q1, Q2]), "operationType" : NewBodyOperationType.ADD, "depth" : 9 * mm});
        }
        {
            var Q0;
            Q0=makeQuery(id+"F0.imprint","IMPRINT",FACE,{"disambiguationData":[TD([[makeQuery(id+"F0.imprint","IMPRINT",EDGE,{"derivedFrom":sQuery(id+"F0.wireOp",EDGE,"uT1mwovh-5eQD-BnlF-feAO-0dE3emI62IxI.bottom")}),-1.0]])]});
            var Q1;
            {var subQ3=sQuery(id+"F0.wireOp",EDGE,"1ef5baf3-e3af-4f52-87de-d7c0688bd6cd0.MirrorCS");Q1=makeQuery(id+"F0.imprint","IMPRINT",FACE,{"disambiguationData":[TD([[makeQuery(id+"F0.imprint","IMPRINT",EDGE,{"derivedFrom":subQ3}),1.0]])]});}
            var Q2;
            Q2=makeQuery(id+"F0.imprint","IMPRINT",FACE,{"disambiguationData":[TD([[makeQuery(id+"F0.imprint","IMPRINT",EDGE,{"derivedFrom":sQuery(id+"F0.wireOp",EDGE,"E18.top")}),1.0]])]});
            var Q3;
            Q3=makeQuery(id+"F0.imprint","IMPRINT",FACE,{"disambiguationData":[TD([[makeQuery(id+"F0.imprint","IMPRINT",EDGE,{"derivedFrom":sQuery(id+"F0.wireOp",EDGE,"E10")}),-1.0]])]});
            extrude(context, id + "F5", {"entities" : qUnion([Q0, Q1, Q2, Q3]), "operationType" : NewBodyOperationType.ADD, "depth" : 9 * mm});
        }
        {
            var Q0;
            {var subQ6=sQuery(id+"F0.wireOp",EDGE,"E3.right");Q0=makeQuery(id+"F0.imprint","IMPRINT",FACE,{"disambiguationData":[TD([[makeQuery(id+"F0.imprint","IMPRINT",EDGE,{"derivedFrom":subQ6}),1.0]])]});}
            var Q1;
            Q1=makeQuery(id+"F0.imprint","IMPRINT",FACE,{"disambiguationData":[TD([[makeQuery(id+"F0.imprint","IMPRINT",EDGE,{"derivedFrom":sQuery(id+"F0.wireOp",EDGE,"E13.top")}),-1.0]])]});
            var Q2;
            Q2=makeQuery(id+"F0.imprint","IMPRINT",FACE,{"disambiguationData":[TD([[makeQuery(id+"F0.imprint","IMPRINT",EDGE,{"derivedFrom":sQuery(id+"F0.wireOp",EDGE,"E59.top")}),1.0]])]});
            var Q3;
            {var subQ4=sQuery(id+"F0.wireOp",EDGE,"bh2TBSKC-lZca-UFdI-Cz0g-q3ueVDpPmDvW");Q3=makeQuery(id+"F0.imprint","IMPRINT",FACE,{"disambiguationData":[TD([[makeQuery(id+"F0.imprint","IMPRINT",EDGE,{"derivedFrom":subQ4}),-1.0]])]});}
            var Q4;
            {var subQ0=sQuery(id+"F0.wireOp",EDGE,"aAU3WPVR-dTA4-j4p2-lR81-kZStPRb89WRg");Q4=makeQuery(id+"F0.imprint","IMPRINT",FACE,{"disambiguationData":[TD([[makeQuery(id+"F0.imprint","IMPRINT",EDGE,{"derivedFrom":subQ0}),1.0]])]});}
            var Q5;
            {var subQ1=sQuery(id+"F0.wireOp",EDGE,"E60");Q5=makeQuery(id+"F0.imprint","IMPRINT",FACE,{"disambiguationData":[TD([[makeQuery(id+"F0.imprint","IMPRINT",EDGE,{"derivedFrom":subQ1}),1.0]])]});}
            extrude(context, id + "F6", {"entities" : qUnion([Q0, Q1, Q2, Q3, Q4, Q5]), "operationType" : NewBodyOperationType.ADD, "depth" : 11 * mm});
        }
        {
            var Q0;
            Q0=makeQuery(id+"F0.imprint","IMPRINT",FACE,{"disambiguationData":[TD([[makeQuery(id+"F0.imprint","IMPRINT",EDGE,{"derivedFrom":sQuery(id+"F0.wireOp",EDGE,"m8BlJ7m1-8Kvg-NByD-qUaL-ijyeYWDLyWWi.bottom")}),-1.0]])]});
            var Q1;
            Q1=makeQuery(id+"F0.imprint","IMPRINT",FACE,{"disambiguationData":[TD([[makeQuery(id+"F0.imprint","IMPRINT",EDGE,{"derivedFrom":sQuery(id+"F0.wireOp",EDGE,"4a1f739e-ceae-433e-ba49-03ff13220d970.MirrorCS")}),1.0]])]});
            var Q2;
            Q2=makeQuery(id+"F0.imprint","IMPRINT",FACE,{"disambiguationData":[TD([[makeQuery(id+"F0.imprint","IMPRINT",EDGE,{"derivedFrom":sQuery(id+"F0.wireOp",EDGE,"wGd95vYe-XLKb-HGh0-dKvB-zlWKZVMUEUro")}),-1.0]])]});
            var Q3;
            Q3=makeQuery(id+"F0.imprint","IMPRINT",FACE,{"disambiguationData":[TD([[makeQuery(id+"F0.imprint","IMPRINT",EDGE,{"derivedFrom":sQuery(id+"F0.wireOp",EDGE,"1814ffd8-f8d0-40ac-826c-0068f174192d0.MirrorC")}),1.0]])]});
            var Q4;
            Q4=makeQuery(id+"F0.imprint","IMPRINT",FACE,{"disambiguationData":[TD([[makeQuery(id+"F0.imprint","IMPRINT",EDGE,{"derivedFrom":sQuery(id+"F0.wireOp",EDGE,"d06qtbmx-Z072-KO1i-DPNR-y8eWfwE2gxHA")}),1.0]])]});
            var Q5;
            Q5=makeQuery(id+"F0.imprint","IMPRINT",FACE,{"disambiguationData":[TD([[makeQuery(id+"F0.imprint","IMPRINT",EDGE,{"derivedFrom":sQuery(id+"F0.wireOp",EDGE,"1432eec9-fd65-44fb-b7b7-fc5124fc1dc10.MirrorC")}),-1.0]])]});
            var Q6;
            Q6=makeQuery(id+"F0.imprint","IMPRINT",FACE,{"disambiguationData":[TD([[makeQuery(id+"F0.imprint","IMPRINT",EDGE,{"derivedFrom":sQuery(id+"F0.wireOp",EDGE,"E16.top")}),1.0]])]});
            var Q7;
            Q7=makeQuery(id+"F0.imprint","IMPRINT",FACE,{"disambiguationData":[TD([[makeQuery(id+"F0.imprint","IMPRINT",EDGE,{"derivedFrom":sQuery(id+"F0.wireOp",EDGE,"E10")}),1.0]])]});
            var Q8;
            Q8=makeQuery(id+"F0.imprint","IMPRINT",FACE,{"disambiguationData":[TD([[makeQuery(id+"F0.imprint","IMPRINT",EDGE,{"derivedFrom":sQuery(id+"F0.wireOp",EDGE,"E12")}),-1.0]])]});
            var Q9;
            Q9=makeQuery(id+"F0.imprint","IMPRINT",FACE,{"disambiguationData":[TD([[makeQuery(id+"F0.imprint","IMPRINT",EDGE,{"derivedFrom":sQuery(id+"F0.wireOp",EDGE,"CNlPZPS4-n7XZ-K8Df-UJ76-HarHJfZSDmJj")}),-1.0]])]});
            var Q10;
            Q10=makeQuery(id+"F0.imprint","IMPRINT",FACE,{"disambiguationData":[TD([[makeQuery(id+"F0.imprint","IMPRINT",EDGE,{"derivedFrom":sQuery(id+"F0.wireOp",EDGE,"E72")}),1.0]])]});
            extrude(context, id + "F7", {"entities" : qUnion([Q0, Q1, Q2, Q3, Q4, Q5, Q6, Q7, Q8, Q9, Q10]), "operationType" : NewBodyOperationType.ADD, "depth" : 5 * mm});
        }
        {
            var Q0;
            {var subQ10=sQuery(id+"F0.wireOp",EDGE,"as5H9wRG-vlFi-IaeT-bpy4-L7joDgvUDys8");Q0=makeQuery(id+"F0.imprint","IMPRINT",FACE,{"disambiguationData":[TD([[makeQuery(id+"F0.imprint","IMPRINT",EDGE,{"derivedFrom":subQ10}),1.0]])]});}
            var Q1;
            {var subQ0=sQuery(id+"F0.wireOp",EDGE,"0W0PAhTs-SbJl-VnCL-KSUR-W3FI7rDldOZW");Q1=makeQuery(id+"F0.imprint","IMPRINT",FACE,{"disambiguationData":[TD([[makeQuery(id+"F0.imprint","IMPRINT",EDGE,{"derivedFrom":subQ0}),1.0]])]});}
            var Q2;
            {var subQ0=sQuery(id+"F0.wireOp",EDGE,"ab4c6ef1-7dad-48e9-8575-7f87cb457dbe0.MirrorCS");Q2=makeQuery(id+"F0.imprint","IMPRINT",FACE,{"disambiguationData":[TD([[makeQuery(id+"F0.imprint","IMPRINT",EDGE,{"derivedFrom":subQ0}),1.0]])]});}
            var Q3;
            {var subQ1=sQuery(id+"F0.wireOp",EDGE,"efb54391-69b0-4f1c-9c84-c88345ef56250.MirrorCS");Q3=makeQuery(id+"F0.imprint","IMPRINT",FACE,{"disambiguationData":[TD([[makeQuery(id+"F0.imprint","IMPRINT",EDGE,{"derivedFrom":subQ1}),-1.0]])]});}
            var Q4;
            Q4=makeQuery(id+"F0.imprint","IMPRINT",FACE,{"disambiguationData":[TD([[makeQuery(id+"F0.imprint","IMPRINT",EDGE,{"derivedFrom":sQuery(id+"F0.wireOp",EDGE,"E15.top")}),-1.0]])]});
            extrude(context, id + "F8", {"entities" : qUnion([Q0, Q1, Q2, Q3, Q4]), "operationType" : NewBodyOperationType.ADD, "depth" : 7 * mm});
        }
        {
            var Q0;
            {var subQ4=sQuery(id+"F0.wireOp",EDGE,"E2.right");Q0=makeQuery(id+"F0.imprint","IMPRINT",FACE,{"disambiguationData":[TD([[makeQuery(id+"F0.imprint","IMPRINT",EDGE,{"derivedFrom":subQ4}),1.0]])]});}
            var Q1;
            {var subQ4=sQuery(id+"F0.wireOp",EDGE,"E2.right");Q1=makeQuery(id+"F0.imprint","IMPRINT",FACE,{"disambiguationData":[TD([[makeQuery(id+"F0.imprint","IMPRINT",EDGE,{"derivedFrom":subQ4}),-1.0]])]});}
            var Q2;
            {var subQ15=sQuery(id+"F0.wireOp",EDGE,"E8");Q2=makeQuery(id+"F0.imprint","IMPRINT",FACE,{"disambiguationData":[TD([[makeQuery(id+"F0.imprint","IMPRINT",EDGE,{"derivedFrom":subQ15}),1.0]])]});}
            var Q3;
            {var subQ0=sQuery(id+"F0.wireOp",EDGE,"E34.right");var subQ3=makeQuery(id+"F0.imprint","IMPRINT",VERTEX,{"derivedFrom":subQ0});Q3=makeQuery(id+"F0.imprint","IMPRINT",FACE,{"disambiguationData":[TD([[makeQuery(id+"F0.imprint","IMPRINT",EDGE,{"disambiguationData":[TD([[subQ3,1.0]])],"derivedFrom":subQ0}),1.0]])]});}
            var Q4;
            {var subQ6=sQuery(id+"F0.wireOp",EDGE,"E34.top");Q4=makeQuery(id+"F0.imprint","IMPRINT",FACE,{"disambiguationData":[TD([[makeQuery(id+"F0.imprint","IMPRINT",EDGE,{"derivedFrom":subQ6}),1.0]])]});}
            var Q5;
            {var subQ30=sQuery(id+"F0.wireOp",EDGE,"E0.right");Q5=makeQuery(id+"F0.imprint","IMPRINT",FACE,{"disambiguationData":[TD([[makeQuery(id+"F0.imprint","IMPRINT",EDGE,{"derivedFrom":subQ30}),-1.0]])]});}
            var Q6;
            Q6=makeQuery(id+"F0.imprint","IMPRINT",FACE,{"disambiguationData":[TD([[makeQuery(id+"F0.imprint","IMPRINT",EDGE,{"derivedFrom":sQuery(id+"F0.wireOp",EDGE,"E41.bottom")}),-1.0]])]});
            var Q7;
            Q7=makeQuery(id+"F0.imprint","IMPRINT",FACE,{"disambiguationData":[TD([[makeQuery(id+"F0.imprint","IMPRINT",EDGE,{"derivedFrom":sQuery(id+"F0.wireOp",EDGE,"E39.bottom")}),1.0]])]});
            var Q8;
            Q8=makeQuery(id+"F0.imprint","IMPRINT",FACE,{"disambiguationData":[TD([[makeQuery(id+"F0.imprint","IMPRINT",EDGE,{"derivedFrom":sQuery(id+"F0.wireOp",EDGE,"E40.bottom")}),1.0]])]});
            var Q9;
            {var subQ0=sQuery(id+"F0.wireOp",EDGE,"E45");var subQ1=sQuery(id+"F0.wireOp",EDGE,"E43");var subQ2=makeQuery(id+"F0.imprint","INTERSECT",VERTEX,{"derivedFrom":[subQ1,subQ0]});Q9=makeQuery(id+"F0.imprint","IMPRINT",FACE,{"disambiguationData":[TD([[makeQuery(id+"F0.imprint","IMPRINT",EDGE,{"disambiguationData":[TD([[subQ2,-1.0]])],"derivedFrom":subQ1}),1.0]])]});}
            var Q10;
            {var subQ12=sQuery(id+"F0.wireOp",EDGE,"E49");Q10=makeQuery(id+"F0.imprint","IMPRINT",FACE,{"disambiguationData":[TD([[makeQuery(id+"F0.imprint","IMPRINT",EDGE,{"derivedFrom":subQ12}),1.0]])]});}
            extrude(context, id + "F9", {"entities" : qUnion([Q0, Q1, Q2, Q3, Q4, Q5, Q6, Q7, Q8, Q9, Q10]), "operationType" : NewBodyOperationType.ADD, "depth" : 15 * mm});
        }
        {
            var Q0;
            {var subQ14=sQuery(id+"F0.wireOp",EDGE,"E0.right");Q0=makeQuery(id+"F0.imprint","IMPRINT",FACE,{"disambiguationData":[TD([[makeQuery(id+"F0.imprint","IMPRINT",EDGE,{"derivedFrom":subQ14}),-1.0]])]});}
            var Q1;
            {var subQ0=sQuery(id+"F0.wireOp",EDGE,"ab46168d-af6e-42de-824f-0888a4270b770.MirrorCS");Q1=makeQuery(id+"F0.imprint","IMPRINT",FACE,{"disambiguationData":[TD([[makeQuery(id+"F0.imprint","IMPRINT",EDGE,{"derivedFrom":subQ0}),-1.0]])]});}
            var Q2;
            {var subQ0=sQuery(id+"F0.wireOp",EDGE,"2A3WI2Tn-8yDx-OZP5-hdhU-zOEgb1ADnAb4.right");Q2=makeQuery(id+"F0.imprint","IMPRINT",FACE,{"disambiguationData":[TD([[makeQuery(id+"F0.imprint","IMPRINT",EDGE,{"derivedFrom":subQ0}),1.0]])]});}
            var Q3;
            {var subQ0=sQuery(id+"F0.wireOp",EDGE,"2A3WI2Tn-8yDx-OZP5-hdhU-zOEgb1ADnAb4.left");Q3=makeQuery(id+"F0.imprint","IMPRINT",FACE,{"disambiguationData":[TD([[makeQuery(id+"F0.imprint","IMPRINT",EDGE,{"derivedFrom":subQ0}),-1.0]])]});}
            var Q4;
            {var subQ0=sQuery(id+"F0.wireOp",EDGE,"KXApSkYF-fskY-EpyV-lEOU-AstEEemZVb44");var subQ1=sQuery(id+"F0.wireOp",EDGE,"2A3WI2Tn-8yDx-OZP5-hdhU-zOEgb1ADnAb4.bottom");var subQ2=makeQuery(id+"F0.imprint","INTERSECT",VERTEX,{"derivedFrom":[subQ1,subQ0]});Q4=makeQuery(id+"F0.imprint","IMPRINT",FACE,{"disambiguationData":[TD([[makeQuery(id+"F0.imprint","IMPRINT",EDGE,{"disambiguationData":[TD([[subQ2,-1.0]])],"derivedFrom":subQ1}),1.0]])]});}
            var Q5;
            {var subQ0=sQuery(id+"F0.wireOp",EDGE,"4bbdbd1b-dbbd-4441-a1b6-6a8d8a8a4ed50.MirrorCS");var subQ1=sQuery(id+"F0.wireOp",EDGE,"c35836a9-8250-4898-909e-bbcbb419c5620.MirrorCS");var subQ2=makeQuery(id+"F0.imprint","INTERSECT",VERTEX,{"derivedFrom":[subQ1,subQ0]});Q5=makeQuery(id+"F0.imprint","IMPRINT",FACE,{"disambiguationData":[TD([[makeQuery(id+"F0.imprint","IMPRINT",EDGE,{"disambiguationData":[TD([[subQ2,-1.0]])],"derivedFrom":subQ1}),1.0]])]});}
            var Q6;
            {var subQ18=sQuery(id+"F0.wireOp",EDGE,"E0.left");Q6=makeQuery(id+"F0.imprint","IMPRINT",FACE,{"disambiguationData":[TD([[makeQuery(id+"F0.imprint","IMPRINT",EDGE,{"derivedFrom":subQ18}),1.0]])]});}
            var Q7;
            {var subQ0=sQuery(id+"F0.wireOp",EDGE,"E26");Q7=makeQuery(id+"F0.imprint","IMPRINT",FACE,{"disambiguationData":[TD([[makeQuery(id+"F0.imprint","IMPRINT",EDGE,{"derivedFrom":subQ0}),1.0]])]});}
            var Q8;
            {var subQ1=sQuery(id+"F0.wireOp",EDGE,"E1.bottom");var subQ3=sQuery(id+"F0.wireOp",EDGE,"ccde40ff-b11f-4aab-b918-d0b542b40a3d0.MirrorC");var subQ4=makeQuery(id+"F0.imprint","INTERSECT",VERTEX,{"disambiguationData":[OD(1.0)],"derivedFrom":[subQ1,subQ3]});Q8=makeQuery(id+"F0.imprint","IMPRINT",FACE,{"disambiguationData":[TD([[makeQuery(id+"F0.imprint","IMPRINT",EDGE,{"disambiguationData":[TD([[subQ4,-1.0]])],"derivedFrom":subQ3}),1.0]])]});}
            var Q9;
            Q9=makeQuery(id+"F0.imprint","IMPRINT",FACE,{"disambiguationData":[TD([[makeQuery(id+"F0.imprint","IMPRINT",EDGE,{"derivedFrom":sQuery(id+"F0.wireOp",EDGE,"E7.top")}),1.0]])]});
            var Q10;
            {var subQ1=sQuery(id+"F0.wireOp",EDGE,"5Q6wE2rV-OooC-G0Wq-JI59-TQ9ywyUS5N0h");Q10=makeQuery(id+"F0.imprint","IMPRINT",FACE,{"disambiguationData":[TD([[makeQuery(id+"F0.imprint","IMPRINT",EDGE,{"derivedFrom":subQ1}),1.0]])]});}
            var Q11;
            Q11=makeQuery(id+"F0.imprint","IMPRINT",FACE,{"disambiguationData":[TD([[makeQuery(id+"F0.imprint","IMPRINT",EDGE,{"derivedFrom":sQuery(id+"F0.wireOp",EDGE,"E75.bottom")}),1.0]])]});
            var Q12;
            Q12=makeQuery(id+"F0.imprint","IMPRINT",FACE,{"disambiguationData":[TD([[makeQuery(id+"F0.imprint","IMPRINT",EDGE,{"derivedFrom":sQuery(id+"F0.wireOp",EDGE,"E74.bottom")}),-1.0]])]});
            var Q13;
            Q13=makeQuery(id+"F0.imprint","IMPRINT",FACE,{"disambiguationData":[TD([[makeQuery(id+"F0.imprint","IMPRINT",EDGE,{"derivedFrom":sQuery(id+"F0.wireOp",EDGE,"E76.bottom")}),-1.0]])]});
            var Q14;
            {var subQ4=sQuery(id+"F0.wireOp",EDGE,"E77.bottom");Q14=makeQuery(id+"F0.imprint","IMPRINT",FACE,{"disambiguationData":[TD([[makeQuery(id+"F0.imprint","IMPRINT",EDGE,{"derivedFrom":subQ4}),1.0]])]});}
            extrude(context, id + "F10", {"entities" : qUnion([Q0, Q1, Q2, Q3, Q4, Q5, Q6, Q7, Q8, Q9, Q10, Q11, Q12, Q13, Q14]), "operationType" : NewBodyOperationType.ADD, "depth" : 42 * mm});
        }
        {
            var Q0;
            Q0=makeQuery(id+"F10.opExtrude","SWEPT_EDGE",EDGE,{"disambiguationData":[OSD([sQuery(id+"F0.wireOp",EDGE,"E47"),sQuery(id+"F0.wireOp",EDGE,"E48")])]});
            var Q1;
            Q1=makeQuery(id+"F10.opExtrude","SWEPT_EDGE",EDGE,{"disambiguationData":[OSD([sQuery(id+"F0.wireOp",EDGE,"E0.right"),sQuery(id+"F0.wireOp",EDGE,"E48")])]});
            var Q2;
            Q2=makeQuery(id+"F10.opExtrude","SWEPT_EDGE",EDGE,{"disambiguationData":[OSD([sQuery(id+"F0.wireOp",EDGE,"5Q6wE2rV-OooC-G0Wq-JI59-TQ9ywyUS5N0h"),sQuery(id+"F0.wireOp",EDGE,"E47")])]});
            var Q3;
            Q3=makeQuery(id+"F10.opExtrude","SWEPT_EDGE",EDGE,{"disambiguationData":[OSD([sQuery(id+"F0.wireOp",EDGE,"E7.left"),sQuery(id+"F0.wireOp",EDGE,"AcNdPE7c-UUq9-6fqG-Pror-XH4mYHztFVZ3")])]});
            var Q4;
            Q4=makeQuery(id+"F10.opExtrude","SWEPT_EDGE",EDGE,{"disambiguationData":[OSD([sQuery(id+"F0.wireOp",EDGE,"E57"),sQuery(id+"F0.wireOp",EDGE,"E58")])]});
            var Q5;
            Q5=makeQuery(id+"F10.opExtrude","SWEPT_EDGE",EDGE,{"disambiguationData":[OSD([sQuery(id+"F0.wireOp",EDGE,"E56"),sQuery(id+"F0.wireOp",EDGE,"E57")])]});
            var Q6;
            Q6=makeQuery(id+"F9.opExtrude","SWEPT_EDGE",EDGE,{"disambiguationData":[OSD([sQuery(id+"F0.wireOp",EDGE,"E38.top"),sQuery(id+"F0.wireOp",EDGE,"E38.right")])]});
            var Q7;
            Q7=makeQuery(id+"F9.opExtrude","SWEPT_EDGE",EDGE,{"disambiguationData":[OSD([sQuery(id+"F0.wireOp",EDGE,"E34.top"),sQuery(id+"F0.wireOp",EDGE,"E34.left")])]});
            fillet(context, id + "F11", {"entities" : qUnion([Q0, Q1, Q2, Q3, Q4, Q5, Q6, Q7]), "radius" : 2 * mm, "tangentPropagation" : true, "allowEdgeOverflow" : false});
        }
        {
            var Q0;
            Q0=makeQuery(id+"F7.opExtrude","CAP_EDGE",EDGE,{"disambiguationData":[OSD([sQuery(id+"F0.wireOp",EDGE,"405d9007-592b-4bd5-90c4-5b4fa10939770.MirrorC")])],"isStart":true});
            var Q1;
            Q1=makeQuery(id+"F7.opExtrude","CAP_EDGE",EDGE,{"disambiguationData":[OSD([sQuery(id+"F0.wireOp",EDGE,"Tc1mQRA5-XLI1-bt0K-3npp-smT2XxA7ujvk")])],"isStart":true});
            var Q2;
            Q2=makeQuery(id+"F7.opExtrude","CAP_EDGE",EDGE,{"disambiguationData":[OSD([sQuery(id+"F0.wireOp",EDGE,"E25")])],"isStart":true});
            chamfer(context, id + "F12", {"entities" : qUnion([Q0, Q1, Q2]), "width" : 4 * mm, "tangentPropagation" : true});
        }
        {
            var Q0;
            Q0=makeQuery(id+"F10.opExtrude","SWEPT_FACE",FACE,{"disambiguationData":[OSD([sQuery(id+"F0.wireOp",EDGE,"E0.right"),sQuery(id+"F0.wireOp",EDGE,"E7.left")])]});
            var sketch = newSketch(context, id + "F13", { "sketchPlane" : qUnion([Q0])});
            skLineSegment(sketch, "E79.bottom", {"start": v(2.5, 40) * mm, "end": v(11.5, 40) * mm});
            skLineSegment(sketch, "E79.top", {"start": v(2.5, 17) * mm, "end": v(11.5, 17) * mm});
            skLineSegment(sketch, "E79.left", {"start": v(2.5, 40) * mm, "end": v(2.5, 17) * mm});
            skLineSegment(sketch, "E79.right", {"start": v(11.5, 40) * mm, "end": v(11.5, 17) * mm});
            skLineSegment(sketch, "E80.bottom", {"start": v(15.42, 40) * mm, "end": v(24.42, 40) * mm});
            skLineSegment(sketch, "E80.top", {"start": v(15.42, 17) * mm, "end": v(24.42, 17) * mm});
            skLineSegment(sketch, "E80.left", {"start": v(15.42, 40) * mm, "end": v(15.42, 17) * mm});
            skLineSegment(sketch, "E80.right", {"start": v(24.42, 40) * mm, "end": v(24.42, 17) * mm});
            skLineSegment(sketch, "E81.bottom", {"start": v(-16, 40) * mm, "end": v(-28, 40) * mm});
            skLineSegment(sketch, "E81.top", {"start": v(-16, 17) * mm, "end": v(-28, 17) * mm});
            skLineSegment(sketch, "E81.left", {"start": v(-16, 40) * mm, "end": v(-16, 17) * mm});
            skLineSegment(sketch, "E81.right", {"start": v(-28, 40) * mm, "end": v(-28, 17) * mm});
            skLineSegment(sketch, "E82", {"start": v(15.42, 36) * mm, "end": v(24.42, 36) * mm});
            skSolve(sketch);
        }
        {
            var Q0;
            Q0=makeQuery(id+"F13.imprint","IMPRINT",FACE,{"disambiguationData":[TD([[makeQuery(id+"F13.imprint","IMPRINT",EDGE,{"derivedFrom":sQuery(id+"F13.wireOp",EDGE,"E79.bottom")}),-1.0]])]});
            var Q1;
            Q1=makeQuery(id+"F13.imprint","IMPRINT",FACE,{"disambiguationData":[TD([[makeQuery(id+"F13.imprint","IMPRINT",EDGE,{"derivedFrom":sQuery(id+"F13.wireOp",EDGE,"E81.bottom")}),1.0]])]});
            var Q2;
            {var subQ0=sQuery(id+"F13.wireOp",EDGE,"E80.bottom");Q2=makeQuery(id+"F13.imprint","IMPRINT",FACE,{"disambiguationData":[TD([[makeQuery(id+"F13.imprint","IMPRINT",EDGE,{"derivedFrom":subQ0}),-1.0]])]});}
            extrude(context, id + "F14", {"entities" : qUnion([Q0, Q1, Q2]), "operationType" : NewBodyOperationType.REMOVE, "endBound" : BoundingType.UP_TO_NEXT, "oppositeDirection" : true, "depth" : 25 * mm});
        }
        {
            var Q0;
            Q0=makeQuery(id+"F2.opExtrude","CAP_EDGE",EDGE,{"disambiguationData":[OSD([sQuery(id+"F0.wireOp",EDGE,"E24")])],"isStart":true});
            fillet(context, id + "F15", {"entities" : qUnion([Q0]), "radius" : 2 * mm, "tangentPropagation" : true, "allowEdgeOverflow" : false});
        }
        {
            var Q0;
            Q0=makeQuery(id+"F0.imprint","IMPRINT",FACE,{"disambiguationData":[TD([[makeQuery(id+"F0.imprint","IMPRINT",EDGE,{"derivedFrom":sQuery(id+"F0.wireOp",EDGE,"E27")}),1.0]])]});
            extrude(context, id + "F16", {"entities" : qUnion([Q0]), "operationType" : NewBodyOperationType.ADD, "depth" : 13 * mm});
        }
        {
            var Q0;
            Q0=makeQuery(id+"F7.opExtrude","CAP_EDGE",EDGE,{"disambiguationData":[OSD([sQuery(id+"F0.wireOp",EDGE,"CNlPZPS4-n7XZ-K8Df-UJ76-HarHJfZSDmJj")])],"isStart":true});
            var Q1;
            Q1=makeQuery(id+"F7.opExtrude","CAP_EDGE",EDGE,{"disambiguationData":[OSD([sQuery(id+"F0.wireOp",EDGE,"E73")])],"isStart":true});
            chamfer(context, id + "F17", {"entities" : qUnion([Q0, Q1]), "width" : 4 * mm, "tangentPropagation" : true});
        }
        {
            var Q0;
            Q0=makeQuery(id+"F16.opExtrude","SWEPT_EDGE",EDGE,{"disambiguationData":[OSD([sQuery(id+"F0.wireOp",EDGE,"E49"),sQuery(id+"F0.wireOp",EDGE,"E50"),sQuery(id+"F0.wireOp",EDGE,"E51")])]});
            var Q1;
            Q1=makeQuery(id+"F6.opExtrude","SWEPT_EDGE",EDGE,{"disambiguationData":[OSD([sQuery(id+"F0.wireOp",EDGE,"E5"),sQuery(id+"F0.wireOp",EDGE,"E22")])]});
            var Q2;
            Q2=makeQuery(id+"F4.opExtrude","SWEPT_EDGE",EDGE,{"disambiguationData":[OSD([sQuery(id+"F0.wireOp",EDGE,"E5"),sQuery(id+"F0.wireOp",EDGE,"E21")])]});
            var Q3;
            Q3=makeQuery(id+"F6.opExtrude","SWEPT_EDGE",EDGE,{"disambiguationData":[OSD([sQuery(id+"F0.wireOp",EDGE,"E4"),sQuery(id+"F0.wireOp",EDGE,"E22")])]});
            var Q4;
            Q4=makeQuery(id+"F16.opExtrude","SWEPT_EDGE",EDGE,{"disambiguationData":[OSD([sQuery(id+"F0.wireOp",EDGE,"E20"),sQuery(id+"F0.wireOp",EDGE,"E27"),sQuery(id+"F0.wireOp",EDGE,"E50")])]});
            var Q5;
            Q5=makeQuery(id+"F4.opExtrude","SWEPT_EDGE",EDGE,{"disambiguationData":[OSD([sQuery(id+"F0.wireOp",EDGE,"E4"),sQuery(id+"F0.wireOp",EDGE,"E21")])]});
            var Q6;
            Q6=makeQuery(id+"F9.opExtrude","SWEPT_EDGE",EDGE,{"disambiguationData":[OSD([sQuery(id+"F0.wireOp",EDGE,"E38.right"),sQuery(id+"F0.wireOp",EDGE,"E45")])]});
            var Q7;
            Q7=makeQuery(id+"F9.opExtrude","SWEPT_EDGE",EDGE,{"disambiguationData":[OSD([sQuery(id+"F0.wireOp",EDGE,"E34.left"),sQuery(id+"F0.wireOp",EDGE,"E45")])]});
            var Q8;
            {var subQ2=sQuery(id+"F0.wireOp",EDGE,"E5");var subQ3=sQuery(id+"F0.wireOp",EDGE,"E34.top");Q8=makeQuery(id+"F55GzlxX9SGPka5_1.boolean.opBoolean","SPLIT",EDGE,{"disambiguationData":[TD([makeQuery(id+"F14.opExtrude","SWEPT_FACE",FACE,{"disambiguationData":[OSD([sQuery(id+"F13.wireOp",EDGE,"E79.top")])]})])],"derivedFrom":makeQuery(id+"F9.opExtrude","SWEPT_EDGE",EDGE,{"disambiguationData":[OSD([subQ2,subQ3,sQuery(id+"F0.wireOp",EDGE,"E34.right")])]})});}
            var Q9;
            Q9=makeQuery(id+"F9.opExtrude","SWEPT_EDGE",EDGE,{"disambiguationData":[OSD([sQuery(id+"F0.wireOp",EDGE,"E4"),sQuery(id+"F0.wireOp",EDGE,"E38.top")])]});
            var Q10;
            Q10=makeQuery(id+"F10.opExtrude","SWEPT_EDGE",EDGE,{"disambiguationData":[OSD([sQuery(id+"F0.wireOp",EDGE,"E45"),sQuery(id+"F0.wireOp",EDGE,"E46")])]});
            var Q11;
            Q11=makeQuery(id+"F10.opExtrude","SWEPT_EDGE",EDGE,{"disambiguationData":[OSD([sQuery(id+"F0.wireOp",EDGE,"E38.left"),sQuery(id+"F0.wireOp",EDGE,"E45")])]});
            var Q12;
            Q12=makeQuery(id+"F10.opExtrude","SWEPT_EDGE",EDGE,{"disambiguationData":[OSD([sQuery(id+"F0.wireOp",EDGE,"E1.right"),sQuery(id+"F0.wireOp",EDGE,"E74.bottom"),sQuery(id+"F0.wireOp",EDGE,"E74.left")])]});
            var Q13;
            Q13=makeQuery(id+"F10.opExtrude","SWEPT_EDGE",EDGE,{"disambiguationData":[OSD([sQuery(id+"F0.wireOp",EDGE,"E43"),sQuery(id+"F0.wireOp",EDGE,"E75.bottom"),sQuery(id+"F0.wireOp",EDGE,"E75.left")])]});
            var Q14;
            Q14=makeQuery(id+"F10.opExtrude","SWEPT_EDGE",EDGE,{"disambiguationData":[OSD([sQuery(id+"F0.wireOp",EDGE,"E53"),sQuery(id+"F0.wireOp",EDGE,"E76.top"),sQuery(id+"F0.wireOp",EDGE,"E76.right")])]});
            var Q15;
            Q15=makeQuery(id+"F10.opExtrude","SWEPT_EDGE",EDGE,{"disambiguationData":[OSD([sQuery(id+"F0.wireOp",EDGE,"E55"),sQuery(id+"F0.wireOp",EDGE,"E78.top")])]});
            var Q16;
            Q16=makeQuery(id+"F10.opExtrude","SWEPT_EDGE",EDGE,{"disambiguationData":[OSD([sQuery(id+"F0.wireOp",EDGE,"E1.right"),sQuery(id+"F0.wireOp",EDGE,"E74.top"),sQuery(id+"F0.wireOp",EDGE,"E74.left")])]});
            var Q17;
            Q17=makeQuery(id+"F10.opExtrude","SWEPT_EDGE",EDGE,{"disambiguationData":[OSD([sQuery(id+"F0.wireOp",EDGE,"E75.top"),sQuery(id+"F0.wireOp",EDGE,"E75.left")])]});
            fillet(context, id + "F18", {"entities" : qUnion([Q0, Q1, Q2, Q3, Q4, Q5, Q6, Q7, Q8, Q9, Q10, Q11, Q12, Q13, Q14, Q15, Q16, Q17]), "radius" : 2.5 * mm, "tangentPropagation" : true, "allowEdgeOverflow" : false});
        }
        {
            var Q0;
            Q0=makeQuery(id+"F18.opFillet","BLEND_EDGE",EDGE,{"blendedFrom":[makeQuery(id+"F10.opExtrude","SWEPT_EDGE",EDGE,{"disambiguationData":[OSD([sQuery(id+"F0.wireOp",EDGE,"E43"),sQuery(id+"F0.wireOp",EDGE,"E75.bottom"),sQuery(id+"F0.wireOp",EDGE,"E75.left")])]}),makeQuery(id+"F10.opExtrude","SWEPT_FACE",FACE,{"disambiguationData":[OSD([sQuery(id+"F0.wireOp",EDGE,"E75.right")])]})],"blendedInto":[makeQuery(id+"F10.opExtrude","SWEPT_FACE",FACE,{"disambiguationData":[OSD([sQuery(id+"F0.wireOp",EDGE,"E75.right")])]})]});
            var Q1;
            Q1=makeQuery(id+"F18.opFillet","BLEND_EDGE",EDGE,{"blendedFrom":[makeQuery(id+"F10.opExtrude","SWEPT_EDGE",EDGE,{"disambiguationData":[OSD([sQuery(id+"F0.wireOp",EDGE,"E1.right"),sQuery(id+"F0.wireOp",EDGE,"E74.bottom"),sQuery(id+"F0.wireOp",EDGE,"E74.left")])]}),makeQuery(id+"F10.opExtrude","SWEPT_FACE",FACE,{"disambiguationData":[OSD([sQuery(id+"F0.wireOp",EDGE,"E74.right")])]})],"blendedInto":[makeQuery(id+"F10.opExtrude","SWEPT_FACE",FACE,{"disambiguationData":[OSD([sQuery(id+"F0.wireOp",EDGE,"E74.right")])]})]});
            var Q2;
            Q2=makeQuery(id+"F10.opExtrude","SWEPT_EDGE",EDGE,{"disambiguationData":[OSD([sQuery(id+"F0.wireOp",EDGE,"E54"),sQuery(id+"F0.wireOp",EDGE,"E76.bottom"),sQuery(id+"F0.wireOp",EDGE,"E76.left")])]});
            var Q3;
            Q3=makeQuery(id+"F10.opExtrude","SWEPT_EDGE",EDGE,{"disambiguationData":[OSD([sQuery(id+"F0.wireOp",EDGE,"E54"),sQuery(id+"F0.wireOp",EDGE,"E77.bottom"),sQuery(id+"F0.wireOp",EDGE,"E78.right")])]});
            fillet(context, id + "F19", {"entities" : qUnion([Q0, Q1, Q2, Q3]), "radius" : 2 * mm, "tangentPropagation" : true, "allowEdgeOverflow" : false});
        }
        {
            var Q0;
            {var subQ0=sQuery(id+"F0.wireOp",EDGE,"E78.right");var subQ1=sQuery(id+"F0.wireOp",EDGE,"E76.left");var subQ2=sQuery(id+"F0.wireOp",EDGE,"E71");var subQ3=sQuery(id+"F0.wireOp",EDGE,"E70");var subQ4=sQuery(id+"F0.wireOp",EDGE,"E62");var subQ5=sQuery(id+"F0.wireOp",EDGE,"E61");var subQ6=sQuery(id+"F0.wireOp",EDGE,"E60");var subQ7=sQuery(id+"F0.wireOp",EDGE,"E59.right");var subQ8=sQuery(id+"F0.wireOp",EDGE,"E59.left");var subQ9=sQuery(id+"F0.wireOp",EDGE,"E59.top");var subQ10=sQuery(id+"F0.wireOp",EDGE,"E59.bottom");var subQ11=sQuery(id+"F0.wireOp",EDGE,"E54");var subQ12=sQuery(id+"F0.wireOp",EDGE,"E52");var subQ13=sQuery(id+"F0.wireOp",EDGE,"E51");var subQ14=sQuery(id+"F0.wireOp",EDGE,"E50");var subQ15=sQuery(id+"F0.wireOp",EDGE,"E27");var subQ16=sQuery(id+"F0.wireOp",EDGE,"E75.left");var subQ17=sQuery(id+"F0.wireOp",EDGE,"E75.right");var subQ18=sQuery(id+"F0.wireOp",EDGE,"E75.top");var subQ19=sQuery(id+"F0.wireOp",EDGE,"E75.bottom");var subQ20=sQuery(id+"F0.wireOp",EDGE,"E78.top");var subQ21=sQuery(id+"F0.wireOp",EDGE,"E76.top");var subQ22=sQuery(id+"F0.wireOp",EDGE,"E74.right");var subQ23=sQuery(id+"F0.wireOp",EDGE,"E74.top");var subQ24=sQuery(id+"F0.wireOp",EDGE,"E74.bottom");var subQ25=sQuery(id+"F0.wireOp",EDGE,"E67");var subQ26=sQuery(id+"F0.wireOp",EDGE,"E66");var subQ27=sQuery(id+"F0.wireOp",EDGE,"E65");var subQ28=sQuery(id+"F0.wireOp",EDGE,"E64");var subQ29=sQuery(id+"F0.wireOp",EDGE,"E58");var subQ30=sQuery(id+"F0.wireOp",EDGE,"E57");var subQ31=sQuery(id+"F0.wireOp",EDGE,"E56");var subQ32=sQuery(id+"F0.wireOp",EDGE,"E55");var subQ33=sQuery(id+"F0.wireOp",EDGE,"E48");var subQ34=sQuery(id+"F0.wireOp",EDGE,"E47");var subQ35=sQuery(id+"F0.wireOp",EDGE,"E45");var subQ36=sQuery(id+"F0.wireOp",EDGE,"E7.left");var subQ37=sQuery(id+"F0.wireOp",EDGE,"E0.right");var subQ38=sQuery(id+"F0.wireOp",EDGE,"E63");var subQ39=sQuery(id+"F0.wireOp",EDGE,"E49");var subQ40=sQuery(id+"F0.wireOp",EDGE,"E38.right");var subQ41=sQuery(id+"F0.wireOp",EDGE,"E38.top");var subQ42=sQuery(id+"F0.wireOp",EDGE,"E34.left");var subQ43=sQuery(id+"F0.wireOp",EDGE,"E34.top");var subQ44=sQuery(id+"F0.wireOp",EDGE,"E20");var subQ45=sQuery(id+"F0.wireOp",EDGE,"E5");var subQ46=sQuery(id+"F0.wireOp",EDGE,"E4");var subQ47=sQuery(id+"F0.wireOp",EDGE,"E31.MirrorC");var subQ48=sQuery(id+"F0.wireOp",EDGE,"E28");var subQ49=sQuery(id+"F0.wireOp",EDGE,"E21");var subQ50=sQuery(id+"F0.wireOp",EDGE,"E16.right");var subQ51=sQuery(id+"F0.wireOp",EDGE,"E16.left");var subQ52=sQuery(id+"F0.wireOp",EDGE,"E16.top");var subQ53=sQuery(id+"F0.wireOp",EDGE,"E16.bottom");var subQ54=sQuery(id+"F0.wireOp",EDGE,"E15.right");var subQ55=sQuery(id+"F0.wireOp",EDGE,"E15.left");var subQ56=sQuery(id+"F0.wireOp",EDGE,"E15.top");var subQ57=sQuery(id+"F0.wireOp",EDGE,"E10");var subQ58=sQuery(id+"F0.wireOp",EDGE,"E33.MirrorC");var subQ59=sQuery(id+"F0.wireOp",EDGE,"E30");var subQ60=sQuery(id+"F0.wireOp",EDGE,"E22");var subQ61=sQuery(id+"F0.wireOp",EDGE,"E18.right");var subQ62=sQuery(id+"F0.wireOp",EDGE,"E18.left");var subQ63=sQuery(id+"F0.wireOp",EDGE,"E18.top");var subQ64=sQuery(id+"F0.wireOp",EDGE,"E18.bottom");var subQ65=sQuery(id+"F0.wireOp",EDGE,"E13.right");var subQ66=sQuery(id+"F0.wireOp",EDGE,"E13.left");var subQ67=sQuery(id+"F0.wireOp",EDGE,"E13.top");var subQ68=sQuery(id+"F0.wireOp",EDGE,"E32.MirrorC");var subQ69=sQuery(id+"F0.wireOp",EDGE,"E29");var subQ70=sQuery(id+"F0.wireOp",EDGE,"E17.right");var subQ71=sQuery(id+"F0.wireOp",EDGE,"E17.left");var subQ72=sQuery(id+"F0.wireOp",EDGE,"E17.top");var subQ73=sQuery(id+"F0.wireOp",EDGE,"E17.bottom");var subQ74=sQuery(id+"F0.wireOp",EDGE,"E14.right");var subQ75=sQuery(id+"F0.wireOp",EDGE,"E14.left");var subQ76=sQuery(id+"F0.wireOp",EDGE,"E14.top");var subQ77=sQuery(id+"F0.wireOp",EDGE,"E11");var subQ78=sQuery(id+"F0.wireOp",EDGE,"E12");var subQ79=sQuery(id+"F0.wireOp",EDGE,"E72");Q0=makeQuery(id+"F16.boolean.opBoolean","MERGE",FACE,{"derivedFrom":[makeQuery(id+"F1.opExtrude","CAP_FACE",FACE,{"disambiguationData":[OSD([subQ5])],"isStart":true}),makeQuery(id+"F1.opExtrude","CAP_FACE",FACE,{"disambiguationData":[OSD([subQ4])],"isStart":true}),makeQuery(id+"F7.boolean.opBoolean","MERGE",FACE,{"derivedFrom":[makeQuery(id+"F6.opExtrude","CAP_FACE",FACE,{"disambiguationData":[OSD([subQ10,subQ9,subQ8,subQ7,subQ6,subQ3,subQ2,subQ79])],"isStart":true}),makeQuery(id+"F7.opExtrude","CAP_FACE",FACE,{"disambiguationData":[OSD([subQ79,sQuery(id+"F0.wireOp",EDGE,"E73")])],"isStart":true})]}),makeQuery(id+"F10.boolean.opBoolean","MERGE",FACE,{"derivedFrom":[makeQuery(id+"F9.boolean.opBoolean","MERGE",FACE,{"derivedFrom":[makeQuery(id+"F8.boolean.opBoolean","MERGE",FACE,{"derivedFrom":[makeQuery(id+"F1.opExtrude","CAP_FACE",FACE,{"disambiguationData":[OSD([subQ45,subQ38,subQ28,subQ27,subQ26,subQ25])],"isStart":true}),makeQuery(id+"F1.opExtrude","CAP_FACE",FACE,{"disambiguationData":[OSD([subQ48])],"isStart":true}),makeQuery(id+"F1.opExtrude","CAP_FACE",FACE,{"disambiguationData":[OSD([subQ47])],"isStart":true}),makeQuery(id+"F7.boolean.opBoolean","MERGE",FACE,{"derivedFrom":[makeQuery(id+"F1.opExtrude","CAP_FACE",FACE,{"disambiguationData":[OSD([subQ78,sQuery(id+"F0.wireOp",EDGE,"E23")])],"isStart":true}),makeQuery(id+"F7.opExtrude","CAP_FACE",FACE,{"disambiguationData":[OSD([subQ78,subQ56,subQ55,subQ54,subQ53,subQ52,subQ51,subQ50])],"isStart":true})]}),makeQuery(id+"F7.boolean.opBoolean","MERGE",FACE,{"derivedFrom":[makeQuery(id+"F6.boolean.opBoolean","MERGE",FACE,{"derivedFrom":[makeQuery(id+"F1.opExtrude","CAP_FACE",FACE,{"disambiguationData":[OSD([subQ59])],"isStart":true}),makeQuery(id+"F1.opExtrude","CAP_FACE",FACE,{"disambiguationData":[OSD([subQ58])],"isStart":true}),makeQuery(id+"F4.boolean.opBoolean","MERGE",FACE,{"derivedFrom":[makeQuery(id+"F1.opExtrude","CAP_FACE",FACE,{"disambiguationData":[OSD([subQ69])],"isStart":true}),makeQuery(id+"F1.opExtrude","CAP_FACE",FACE,{"disambiguationData":[OSD([subQ68])],"isStart":true}),makeQuery(id+"F3.boolean.opBoolean","MERGE",FACE,{"derivedFrom":[makeQuery(id+"F2.opExtrude","CAP_FACE",FACE,{"disambiguationData":[OSD([subQ77,sQuery(id+"F0.wireOp",EDGE,"E24")])],"isStart":true}),makeQuery(id+"F3.opExtrude","CAP_FACE",FACE,{"disambiguationData":[OSD([subQ77,subQ76,subQ75,subQ74,subQ73,subQ72,subQ71,subQ70])],"isStart":true})]}),makeQuery(id+"F4.opExtrude","CAP_FACE",FACE,{"disambiguationData":[OSD([subQ46,subQ45,subQ76,subQ75,subQ74,subQ73,subQ72,subQ71,subQ70,subQ49,subQ60,subQ69,subQ68])],"isStart":true})]}),makeQuery(id+"F5.opExtrude","CAP_FACE",FACE,{"disambiguationData":[OSD([subQ57,subQ67,subQ66,subQ65,subQ64,subQ63,subQ62,subQ61])],"isStart":true}),makeQuery(id+"F6.opExtrude","CAP_FACE",FACE,{"disambiguationData":[OSD([subQ46,subQ45,subQ67,subQ66,subQ65,subQ64,subQ63,subQ62,subQ61,subQ44,subQ60,subQ59,subQ58,subQ39,subQ14])],"isStart":true})]}),makeQuery(id+"F7.opExtrude","CAP_FACE",FACE,{"disambiguationData":[OSD([subQ57,sQuery(id+"F0.wireOp",EDGE,"E25")])],"isStart":true})]}),makeQuery(id+"F8.opExtrude","CAP_FACE",FACE,{"disambiguationData":[OSD([subQ46,subQ45,subQ56,subQ55,subQ54,subQ53,subQ52,subQ51,subQ50,subQ49,subQ48,subQ47,subQ43,subQ42,subQ41,subQ40,subQ35])],"isStart":true})]}),makeQuery(id+"F9.opExtrude","CAP_FACE",FACE,{"disambiguationData":[OSD([subQ37,subQ46,subQ45,subQ36,subQ44,subQ15,subQ43,subQ42,sQuery(id+"F0.wireOp",EDGE,"E36"),sQuery(id+"F0.wireOp",EDGE,"E37.MirrorC"),subQ41,subQ40,subQ35,subQ34,subQ33,subQ39,subQ13,subQ12,subQ11,subQ32,subQ31,subQ30,subQ29,subQ38,subQ28,subQ27,subQ26,subQ25,subQ24,subQ23,sQuery(id+"F0.wireOp",EDGE,"E74.left"),subQ22,subQ19,subQ18,subQ17,subQ16,sQuery(id+"F0.wireOp",EDGE,"E76.bottom"),subQ21,sQuery(id+"F0.wireOp",EDGE,"E76.right"),sQuery(id+"F0.wireOp",EDGE,"E77.bottom"),subQ20])],"isStart":true})]}),makeQuery(id+"F10.opExtrude","CAP_FACE",FACE,{"disambiguationData":[OSD([subQ37,sQuery(id+"F0.wireOp",EDGE,"E1.right"),subQ36,sQuery(id+"F0.wireOp",EDGE,"E8"),sQuery(id+"F0.wireOp",EDGE,"E35.left"),sQuery(id+"F0.wireOp",EDGE,"E38.left"),sQuery(id+"F0.wireOp",EDGE,"E39.bottom"),sQuery(id+"F0.wireOp",EDGE,"E39.top"),sQuery(id+"F0.wireOp",EDGE,"E39.right"),sQuery(id+"F0.wireOp",EDGE,"E40.bottom"),sQuery(id+"F0.wireOp",EDGE,"E40.top"),sQuery(id+"F0.wireOp",EDGE,"E40.right"),sQuery(id+"F0.wireOp",EDGE,"E41.bottom"),sQuery(id+"F0.wireOp",EDGE,"E41.top"),sQuery(id+"F0.wireOp",EDGE,"E41.right"),sQuery(id+"F0.wireOp",EDGE,"E43"),subQ35,sQuery(id+"F0.wireOp",EDGE,"E46"),subQ34,subQ33,sQuery(id+"F0.wireOp",EDGE,"E53"),subQ11,subQ32,subQ31,subQ30,subQ29,subQ28,subQ27,subQ26,subQ25,subQ24,subQ23,subQ22,subQ21,subQ1,subQ20,subQ0])],"isStart":true}),makeQuery(id+"F10.opExtrude","CAP_FACE",FACE,{"disambiguationData":[OSD([subQ19,subQ18,subQ17,subQ16])],"isStart":true})]}),makeQuery(id+"F16.opExtrude","CAP_FACE",FACE,{"disambiguationData":[OSD([subQ15,subQ14,subQ13,subQ12,subQ11,subQ10,subQ9,subQ8,subQ7,subQ6,subQ5,subQ4,subQ3,subQ2,subQ1,subQ0])],"isStart":true})]});}
            var sketch = newSketch(context, id + "F20", { "sketchPlane" : qUnion([Q0])});
            skCircle(sketch, "E83", {"center": v(-28.17, -32.5) * mm, "radius": 5.5 * mm});
            skCircle(sketch, "E84", {"center": v(-4.97, -32.54) * mm, "radius": 5.5 * mm});
            skCircle(sketch, "E85", {"center": v(-4.97, 59.78) * mm, "radius": 5.5 * mm});
            skCircle(sketch, "E86", {"center": v(-28.17, 59.78) * mm, "radius": 5.5 * mm});
            skSolve(sketch);
        }
        {
            var Q0;
            Q0=makeQuery(id+"F20.imprint","IMPRINT",FACE,{"disambiguationData":[TD([[makeQuery(id+"F20.imprint","IMPRINT",EDGE,{"derivedFrom":sQuery(id+"F20.wireOp",EDGE,"E86")}),1.0]])]});
            var Q1;
            Q1=makeQuery(id+"F20.imprint","IMPRINT",FACE,{"disambiguationData":[TD([[makeQuery(id+"F20.imprint","IMPRINT",EDGE,{"derivedFrom":sQuery(id+"F20.wireOp",EDGE,"E85")}),1.0]])]});
            var Q2;
            Q2=makeQuery(id+"F20.imprint","IMPRINT",FACE,{"disambiguationData":[TD([[makeQuery(id+"F20.imprint","IMPRINT",EDGE,{"derivedFrom":sQuery(id+"F20.wireOp",EDGE,"E83")}),1.0]])]});
            var Q3;
            Q3=makeQuery(id+"F20.imprint","IMPRINT",FACE,{"disambiguationData":[TD([[makeQuery(id+"F20.imprint","IMPRINT",EDGE,{"derivedFrom":sQuery(id+"F20.wireOp",EDGE,"E84")}),1.0]])]});
            extrude(context, id + "F21", {"entities" : qUnion([Q0, Q1, Q2, Q3]), "operationType" : NewBodyOperationType.REMOVE, "oppositeDirection" : true, "depth" : 2 * mm});
        }
        {
            var Q0;
            Q0=makeQuery(id+"F10.boolean.opBoolean","MERGE",FACE,{"derivedFrom":[makeQuery(id+"F10.opExtrude","CAP_FACE",FACE,{"disambiguationData":[OSD([sQuery(id+"F0.wireOp",EDGE,"E0.right"),sQuery(id+"F0.wireOp",EDGE,"E1.right"),sQuery(id+"F0.wireOp",EDGE,"E7.left"),sQuery(id+"F0.wireOp",EDGE,"E8"),sQuery(id+"F0.wireOp",EDGE,"E35.left"),sQuery(id+"F0.wireOp",EDGE,"E38.left"),sQuery(id+"F0.wireOp",EDGE,"E39.bottom"),sQuery(id+"F0.wireOp",EDGE,"E39.top"),sQuery(id+"F0.wireOp",EDGE,"E39.right"),sQuery(id+"F0.wireOp",EDGE,"E40.bottom"),sQuery(id+"F0.wireOp",EDGE,"E40.top"),sQuery(id+"F0.wireOp",EDGE,"E40.right"),sQuery(id+"F0.wireOp",EDGE,"E41.bottom"),sQuery(id+"F0.wireOp",EDGE,"E41.top"),sQuery(id+"F0.wireOp",EDGE,"E41.right"),sQuery(id+"F0.wireOp",EDGE,"E43"),sQuery(id+"F0.wireOp",EDGE,"E45"),sQuery(id+"F0.wireOp",EDGE,"E46"),sQuery(id+"F0.wireOp",EDGE,"E47"),sQuery(id+"F0.wireOp",EDGE,"E48"),sQuery(id+"F0.wireOp",EDGE,"E53"),sQuery(id+"F0.wireOp",EDGE,"E54"),sQuery(id+"F0.wireOp",EDGE,"E55"),sQuery(id+"F0.wireOp",EDGE,"E56"),sQuery(id+"F0.wireOp",EDGE,"E57"),sQuery(id+"F0.wireOp",EDGE,"E58"),sQuery(id+"F0.wireOp",EDGE,"E64"),sQuery(id+"F0.wireOp",EDGE,"E65"),sQuery(id+"F0.wireOp",EDGE,"E66"),sQuery(id+"F0.wireOp",EDGE,"E67"),sQuery(id+"F0.wireOp",EDGE,"E74.bottom"),sQuery(id+"F0.wireOp",EDGE,"E74.top"),sQuery(id+"F0.wireOp",EDGE,"E74.right"),sQuery(id+"F0.wireOp",EDGE,"E76.top"),sQuery(id+"F0.wireOp",EDGE,"E76.left"),sQuery(id+"F0.wireOp",EDGE,"E78.top"),sQuery(id+"F0.wireOp",EDGE,"E78.right")])],"isStart":false}),makeQuery(id+"F10.opExtrude","CAP_FACE",FACE,{"disambiguationData":[OSD([sQuery(id+"F0.wireOp",EDGE,"E75.bottom"),sQuery(id+"F0.wireOp",EDGE,"E75.top"),sQuery(id+"F0.wireOp",EDGE,"E75.right"),sQuery(id+"F0.wireOp",EDGE,"E75.left")])],"isStart":false})]});
            var sketch = newSketch(context, id + "F22", { "sketchPlane" : qUnion([Q0])});
            skCircle(sketch, "E87", {"center": v(0, -63.2) * mm, "radius": 1.5 * mm});
            skCircle(sketch, "E88", {"center": v(-32.07, -63.2) * mm, "radius": 1.5 * mm});
            skCircle(sketch, "E89", {"center": v(-32.07, -33) * mm, "radius": 1.5 * mm});
            skCircle(sketch, "E90", {"center": v(0, -33) * mm, "radius": 1.5 * mm});
            skSolve(sketch);
        }
        {
            var Q0;
            Q0=makeQuery(id+"F22.imprint","IMPRINT",FACE,{"disambiguationData":[TD([[makeQuery(id+"F22.imprint","IMPRINT",EDGE,{"derivedFrom":sQuery(id+"F22.wireOp",EDGE,"E89")}),1.0]])]});
            var Q1;
            Q1=makeQuery(id+"F22.imprint","IMPRINT",FACE,{"disambiguationData":[TD([[makeQuery(id+"F22.imprint","IMPRINT",EDGE,{"derivedFrom":sQuery(id+"F22.wireOp",EDGE,"E90")}),1.0]])]});
            var Q2;
            Q2=makeQuery(id+"F22.imprint","IMPRINT",FACE,{"disambiguationData":[TD([[makeQuery(id+"F22.imprint","IMPRINT",EDGE,{"derivedFrom":sQuery(id+"F22.wireOp",EDGE,"E87")}),1.0]])]});
            var Q3;
            Q3=makeQuery(id+"F22.imprint","IMPRINT",FACE,{"disambiguationData":[TD([[makeQuery(id+"F22.imprint","IMPRINT",EDGE,{"derivedFrom":sQuery(id+"F22.wireOp",EDGE,"E88")}),1.0]])]});
            extrude(context, id + "F23", {"entities" : qUnion([Q0, Q1, Q2, Q3]), "operationType" : NewBodyOperationType.REMOVE, "oppositeDirection" : true, "depth" : 25 * mm});
        }
        {
            var Q0;
            {var subQ0=sQuery(id+"F0.wireOp",EDGE,"E55");var subQ1=sQuery(id+"F0.wireOp",EDGE,"E65");var subQ2=sQuery(id+"F0.wireOp",EDGE,"E64");var subQ3=sQuery(id+"F0.wireOp",EDGE,"E51");var subQ4=sQuery(id+"F0.wireOp",EDGE,"E49");var subQ5=sQuery(id+"F0.wireOp",EDGE,"E5");var subQ6=sQuery(id+"F0.wireOp",EDGE,"E75.right");var subQ7=sQuery(id+"F0.wireOp",EDGE,"E75.bottom");var subQ8=sQuery(id+"F0.wireOp",EDGE,"E75.top");var subQ9=sQuery(id+"F0.wireOp",EDGE,"E78.top");Q0=makeQuery(id+"F10.boolean.opBoolean","SPLIT",FACE,{"disambiguationData":[TD([makeQuery(id+"F10.opExtrude","SWEPT_FACE",FACE,{"disambiguationData":[OSD([sQuery(id+"F0.wireOp",EDGE,"E43")])]})])],"derivedFrom":makeQuery(id+"F9.opExtrude","CAP_FACE",FACE,{"disambiguationData":[OSD([sQuery(id+"F0.wireOp",EDGE,"E0.right"),sQuery(id+"F0.wireOp",EDGE,"E4"),subQ5,sQuery(id+"F0.wireOp",EDGE,"E7.left"),sQuery(id+"F0.wireOp",EDGE,"E20"),sQuery(id+"F0.wireOp",EDGE,"E27"),sQuery(id+"F0.wireOp",EDGE,"E34.top"),sQuery(id+"F0.wireOp",EDGE,"E34.left"),sQuery(id+"F0.wireOp",EDGE,"E36"),sQuery(id+"F0.wireOp",EDGE,"E37.MirrorC"),sQuery(id+"F0.wireOp",EDGE,"E38.top"),sQuery(id+"F0.wireOp",EDGE,"E38.right"),sQuery(id+"F0.wireOp",EDGE,"E45"),sQuery(id+"F0.wireOp",EDGE,"E47"),sQuery(id+"F0.wireOp",EDGE,"E48"),subQ4,subQ3,sQuery(id+"F0.wireOp",EDGE,"E52"),sQuery(id+"F0.wireOp",EDGE,"E54"),subQ0,sQuery(id+"F0.wireOp",EDGE,"E56"),sQuery(id+"F0.wireOp",EDGE,"E57"),sQuery(id+"F0.wireOp",EDGE,"E58"),sQuery(id+"F0.wireOp",EDGE,"E63"),subQ2,subQ1,sQuery(id+"F0.wireOp",EDGE,"E66"),sQuery(id+"F0.wireOp",EDGE,"E67"),sQuery(id+"F0.wireOp",EDGE,"E74.bottom"),sQuery(id+"F0.wireOp",EDGE,"E74.top"),sQuery(id+"F0.wireOp",EDGE,"E74.left"),sQuery(id+"F0.wireOp",EDGE,"E74.right"),subQ7,subQ8,subQ6,sQuery(id+"F0.wireOp",EDGE,"E75.left"),sQuery(id+"F0.wireOp",EDGE,"E76.bottom"),sQuery(id+"F0.wireOp",EDGE,"E76.top"),sQuery(id+"F0.wireOp",EDGE,"E76.right"),sQuery(id+"F0.wireOp",EDGE,"E77.bottom"),subQ9])],"isStart":false})});}
            var sketch = newSketch(context, id + "F24", { "sketchPlane" : qUnion([Q0])});
            skCircle(sketch, "E91", {"center": v(-28.1, -25.5) * mm, "radius": 3.5 * mm});
            skLineSegment(sketch, "E92", {"start": v(-28.1, -25.5) * mm, "end": v(-28.1, 35.37) * mm, "construction": true});
            skLineSegment(sketch, "E93", {"start": v(-28.1, 35.37) * mm, "end": v(-5.1, 35.37) * mm, "construction": true});
            skLineSegment(sketch, "E94", {"start": v(-5.1, 35.37) * mm, "end": v(-5.1, -28.71) * mm, "construction": true});
            skCircle(sketch, "E95", {"center": v(-5.1, -25.5) * mm, "radius": 3.5 * mm});
            skSolve(sketch);
        }
        {
            var Q0;
            Q0=makeQuery(id+"F24.imprint","IMPRINT",FACE,{"disambiguationData":[TD([[makeQuery(id+"F24.imprint","IMPRINT",EDGE,{"derivedFrom":sQuery(id+"F24.wireOp",EDGE,"E91")}),1.0]])]});
            var Q1;
            {var subQ0=sQuery(id+"F24.wireOp",EDGE,"E95");var subQ1=makeQuery(id+"F9.opExtrude","CAP_EDGE",EDGE,{"disambiguationData":[OSD([sQuery(id+"F0.wireOp",EDGE,"E5"),sQuery(id+"F0.wireOp",EDGE,"E49"),sQuery(id+"F0.wireOp",EDGE,"E51")])],"isStart":false});var subQ2=makeQuery(id+"F24.imprint","INTERSECT",VERTEX,{"disambiguationData":[OD(0.0)],"derivedFrom":[subQ1,subQ0]});Q1=makeQuery(id+"F24.imprint","IMPRINT",FACE,{"disambiguationData":[TD([[makeQuery(id+"F24.imprint","IMPRINT",EDGE,{"disambiguationData":[TD([[subQ2,1.0]])],"derivedFrom":subQ0}),1.0]])]});}
            var Q2;
            {var subQ0=sQuery(id+"F24.wireOp",EDGE,"E95");var subQ1=makeQuery(id+"F9.opExtrude","CAP_EDGE",EDGE,{"disambiguationData":[OSD([sQuery(id+"F0.wireOp",EDGE,"E5"),sQuery(id+"F0.wireOp",EDGE,"E49"),sQuery(id+"F0.wireOp",EDGE,"E51")])],"isStart":false});var subQ2=makeQuery(id+"F24.imprint","INTERSECT",VERTEX,{"disambiguationData":[OD(0.0)],"derivedFrom":[subQ1,subQ0]});Q2=makeQuery(id+"F24.imprint","IMPRINT",FACE,{"disambiguationData":[TD([[makeQuery(id+"F24.imprint","IMPRINT",EDGE,{"disambiguationData":[TD([[subQ2,-1.0]])],"derivedFrom":subQ0}),1.0]])]});}
            extrude(context, id + "F25", {"entities" : qUnion([Q0, Q1, Q2]), "operationType" : NewBodyOperationType.REMOVE, "oppositeDirection" : true, "depth" : 3 * mm});
        }
    });
